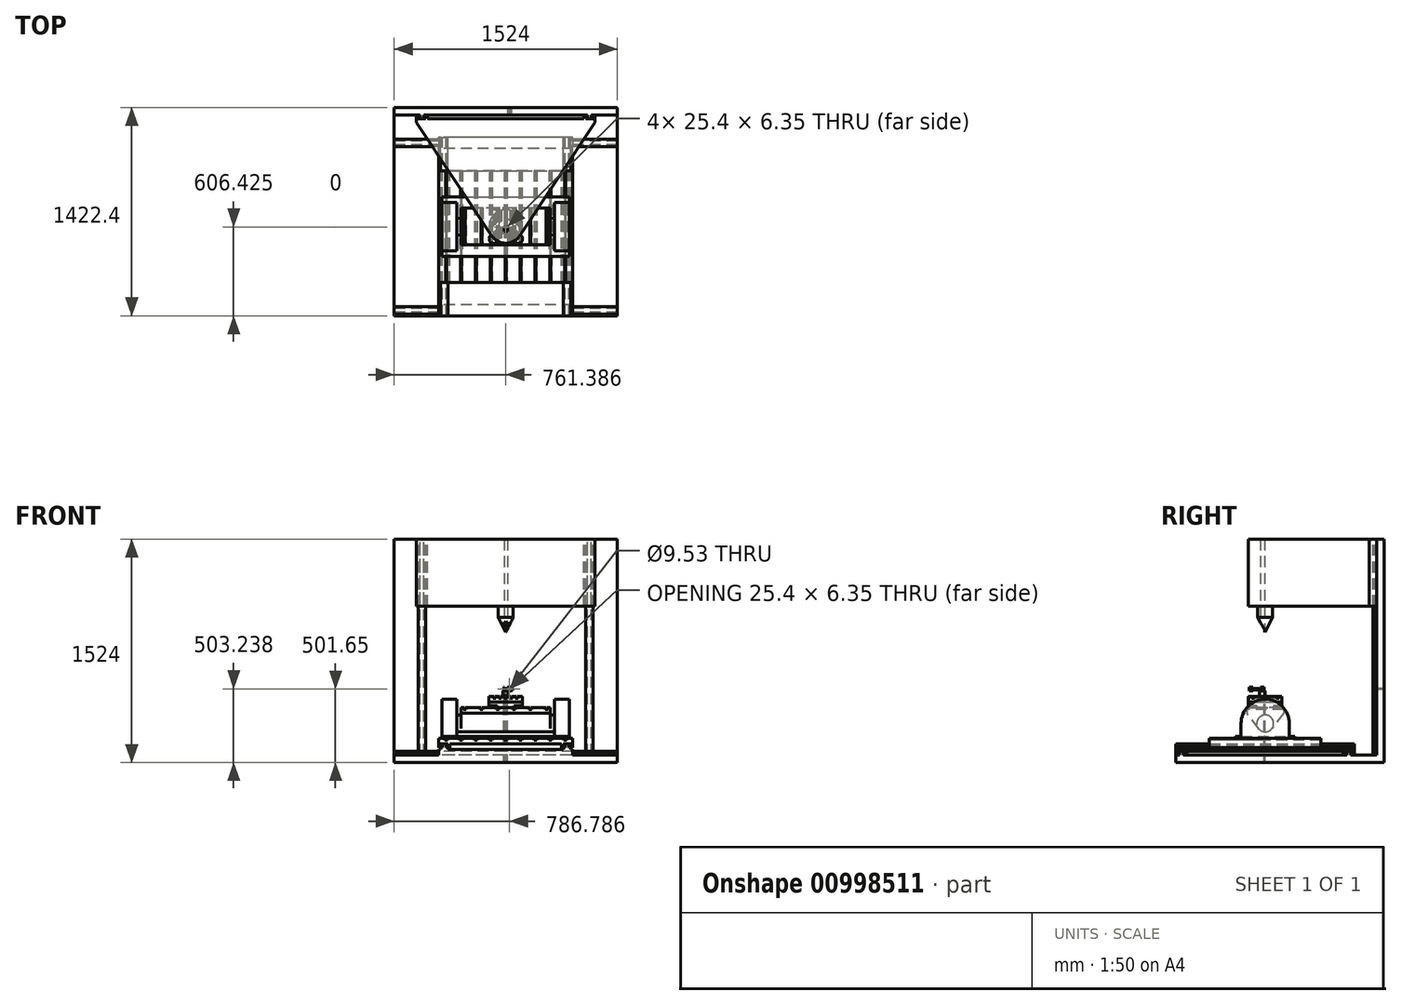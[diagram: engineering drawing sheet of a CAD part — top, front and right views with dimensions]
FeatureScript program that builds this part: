
annotation { "Feature Type Name" : "Feature", "Feature Type Description" : "" }
export const myFeature = defineFeature(function(context is Context, id is Id, definition is map)
    precondition{}
    {
        {
            var Q0;
            Q0=qCreatedBy(makeId("Right.planeOp"),FACE);
            var sketch = newSketch(context, id + "F0", { "sketchPlane" : qUnion([Q0])});
            skLineSegment(sketch, "E0.bottom", {"start": v(-596.9, 0) * mm, "end": v(-546.1, 0) * mm});
            skLineSegment(sketch, "E0.top", {"start": v(-596.9, 12.7) * mm, "end": v(-546.1, 12.7) * mm});
            skLineSegment(sketch, "E0.left", {"start": v(-596.9, 0) * mm, "end": v(-596.9, 12.7) * mm});
            skLineSegment(sketch, "E0.right", {"start": v(-546.1, 0) * mm, "end": v(-546.1, 12.7) * mm});
            skLineSegment(sketch, "E1", {"start": v(0, 50.8) * mm, "end": v(0, 0) * mm, "construction": true});
            skLineSegment(sketch, "E2.bottom", {"start": v(-584.2, 0) * mm, "end": v(-558.8, 0) * mm});
            skLineSegment(sketch, "E2.top", {"start": v(-584.2, -12.7) * mm, "end": v(-558.8, -12.7) * mm});
            skLineSegment(sketch, "E2.left", {"start": v(-584.2, 0) * mm, "end": v(-584.2, -12.7) * mm});
            skLineSegment(sketch, "E2.right", {"start": v(-558.8, 0) * mm, "end": v(-558.8, -12.7) * mm});
            skLineSegment(sketch, "E3.MirrorCS", {"start": v(558.8, 0) * mm, "end": v(558.8, -12.7) * mm});
            skLineSegment(sketch, "E4.MirrorCS", {"start": v(584.2, -12.7) * mm, "end": v(558.8, -12.7) * mm});
            skLineSegment(sketch, "E5.MirrorCS", {"start": v(584.2, 0) * mm, "end": v(558.8, 0) * mm});
            skLineSegment(sketch, "E6.MirrorCS", {"start": v(596.9, 0) * mm, "end": v(546.1, 0) * mm});
            skLineSegment(sketch, "E7.MirrorCS", {"start": v(596.9, 0) * mm, "end": v(596.9, 12.7) * mm});
            skLineSegment(sketch, "E8.MirrorCS", {"start": v(546.1, 0) * mm, "end": v(546.1, 12.7) * mm});
            skLineSegment(sketch, "E9.MirrorCS", {"start": v(584.2, 0) * mm, "end": v(584.2, -12.7) * mm});
            skLineSegment(sketch, "E10.MirrorCS", {"start": v(596.9, 12.7) * mm, "end": v(546.1, 12.7) * mm});
            skLineSegment(sketch, "E11.bottom", {"start": v(-609.6, -12.7) * mm, "end": v(609.6, -12.7) * mm});
            skLineSegment(sketch, "E11.top", {"start": v(-609.6, -63.5) * mm, "end": v(609.6, -63.5) * mm});
            skLineSegment(sketch, "E11.left", {"start": v(-609.6, -12.7) * mm, "end": v(-609.6, -63.5) * mm});
            skLineSegment(sketch, "E11.right", {"start": v(609.6, -12.7) * mm, "end": v(609.6, -63.5) * mm});
            skSolve(sketch);
        }
        {
            var Q0;
            {var subQ6=sQuery(id+"F0.wireOp",EDGE,"E2.top");var subQ7=makeQuery(id+"F0.imprint","IMPRINT",EDGE,{"derivedFrom":subQ6});var subQ10=sQuery(id+"F0.wireOp",EDGE,"E5.MirrorCS");var subQ11=sQuery(id+"F0.wireOp",EDGE,"E3.MirrorCS");var subQ14=makeQuery(id+"F0.imprint","IMPRINT",EDGE,{"derivedFrom":subQ10});Q0=qUnion([makeQuery(id+"F0.imprint","IMPRINT",FACE,{"disambiguationData":[TD([[subQ7,-1.0]])]}),makeQuery(id+"F0.imprint","IMPRINT",FACE,{"disambiguationData":[TD([[makeQuery(id+"F0.imprint","IMPRINT",EDGE,{"derivedFrom":sQuery(id+"F0.wireOp",EDGE,"E0.top")}),-1.0]])]}),makeQuery(id+"F0.imprint","IMPRINT",FACE,{"disambiguationData":[TD([[makeQuery(id+"F0.imprint","IMPRINT",EDGE,{"derivedFrom":subQ11}),1.0]])]}),makeQuery(id+"F0.imprint","IMPRINT",FACE,{"disambiguationData":[TD([[subQ14,-1.0]])]}),makeQuery(id+"F0.imprint","IMPRINT",FACE,{"disambiguationData":[TD([[subQ7,1.0]])]})]);}
            extrude(context, id + "F1", {"entities" : qUnion([Q0]), "depth" : 1524 * mm, "offsetDistance" : 25.4 * mm, "symmetric" : true});
        }
        {
            var Q0;
            Q0=qCreatedBy(makeId("Right.planeOp"),FACE);
            var sketch = newSketch(context, id + "F2", { "sketchPlane" : qUnion([Q0])});
            skLineSegment(sketch, "E12.0", {"start": v(-609.6, -12.7) * mm, "end": v(-584.2, -12.7) * mm});
            skLineSegment(sketch, "E13.0", {"start": v(-584.2, 0) * mm, "end": v(-584.2, -12.7) * mm});
            skLineSegment(sketch, "E14.0", {"start": v(-596.9, 0) * mm, "end": v(-584.2, 0) * mm});
            skLineSegment(sketch, "E15.0", {"start": v(-596.9, 0) * mm, "end": v(-596.9, 12.7) * mm});
            skLineSegment(sketch, "E16.0", {"start": v(-596.9, 12.7) * mm, "end": v(-546.1, 12.7) * mm});
            skLineSegment(sketch, "E17.0", {"start": v(-546.1, 0) * mm, "end": v(-546.1, 12.7) * mm});
            skLineSegment(sketch, "E18.0", {"start": v(-558.8, 0) * mm, "end": v(-546.1, 0) * mm});
            skLineSegment(sketch, "E19.0", {"start": v(-558.8, 0) * mm, "end": v(-558.8, -12.7) * mm});
            skLineSegment(sketch, "E20.0", {"start": v(558.8, 0) * mm, "end": v(558.8, -12.7) * mm});
            skLineSegment(sketch, "E21.0", {"start": v(558.8, 0) * mm, "end": v(546.1, 0) * mm});
            skLineSegment(sketch, "E22.0", {"start": v(546.1, 0) * mm, "end": v(546.1, 12.7) * mm});
            skLineSegment(sketch, "E23.0", {"start": v(596.9, 12.7) * mm, "end": v(546.1, 12.7) * mm});
            skLineSegment(sketch, "E24.0", {"start": v(596.9, 0) * mm, "end": v(596.9, 12.7) * mm});
            skLineSegment(sketch, "E25.0", {"start": v(596.9, 0) * mm, "end": v(584.2, 0) * mm});
            skLineSegment(sketch, "E26.0", {"start": v(584.2, 0) * mm, "end": v(584.2, -12.7) * mm});
            skLineSegment(sketch, "E27.0", {"start": v(584.2, -12.7) * mm, "end": v(609.6, -12.7) * mm});
            skLineSegment(sketch, "E28", {"start": v(-609.6, -12.7) * mm, "end": v(-609.6, 25.4) * mm});
            skLineSegment(sketch, "E29", {"start": v(-609.6, 25.4) * mm, "end": v(609.6, 25.4) * mm});
            skLineSegment(sketch, "E30", {"start": v(609.6, 25.4) * mm, "end": v(609.6, -12.7) * mm});
            skLineSegment(sketch, "E31", {"start": v(-558.8, -12.7) * mm, "end": v(-533.4, -12.7) * mm});
            skLineSegment(sketch, "E32", {"start": v(-533.4, -12.7) * mm, "end": v(-533.4, 12.7) * mm});
            skLineSegment(sketch, "E33", {"start": v(-533.4, 12.7) * mm, "end": v(533.4, 12.7) * mm});
            skLineSegment(sketch, "E34", {"start": v(533.4, 12.7) * mm, "end": v(533.4, -12.7) * mm});
            skLineSegment(sketch, "E35", {"start": v(533.4, -12.7) * mm, "end": v(558.8, -12.7) * mm});
            skSolve(sketch);
        }
        {
            var Q0;
            Q0 = qSketchRegion(id + "F2", true);
            extrude(context, id + "F3", {"entities" : qUnion([Q0]), "depth" : 914.4 * mm, "offsetDistance" : 25.4 * mm, "symmetric" : true});
        }
        {
            var Q0;
            Q0=qCreatedBy(makeId("Front.planeOp"),FACE);
            var sketch = newSketch(context, id + "F4", { "sketchPlane" : qUnion([Q0])});
            skLineSegment(sketch, "E36", {"start": v(0, 0) * mm, "end": v(0, 50.8) * mm, "construction": true});
            skPoint(sketch, "E37.0", {"position": v(-444.5, 25.4) * mm});
            skLineSegment(sketch, "E38", {"start": v(-444.5, 25.4) * mm, "end": v(-444.5, 38.1) * mm});
            skLineSegment(sketch, "E39", {"start": v(-444.5, 38.1) * mm, "end": v(-431.8, 38.1) * mm});
            skLineSegment(sketch, "E40", {"start": v(-431.8, 38.1) * mm, "end": v(-431.8, 50.8) * mm});
            skLineSegment(sketch, "E41", {"start": v(-431.8, 50.8) * mm, "end": v(-444.5, 50.8) * mm});
            skLineSegment(sketch, "E42", {"start": v(-444.5, 50.8) * mm, "end": v(-444.5, 63.5) * mm});
            skLineSegment(sketch, "E43", {"start": v(-444.5, 63.5) * mm, "end": v(-393.7, 63.5) * mm});
            skLineSegment(sketch, "E44", {"start": v(-393.7, 63.5) * mm, "end": v(-393.7, 50.8) * mm});
            skLineSegment(sketch, "E45", {"start": v(-393.7, 50.8) * mm, "end": v(-406.4, 50.8) * mm});
            skLineSegment(sketch, "E46", {"start": v(-406.4, 50.8) * mm, "end": v(-406.4, 38.1) * mm});
            skLineSegment(sketch, "E47", {"start": v(-406.4, 38.1) * mm, "end": v(-393.7, 38.1) * mm});
            skLineSegment(sketch, "E48", {"start": v(-393.7, 38.1) * mm, "end": v(-393.7, 25.4) * mm});
            skLineSegment(sketch, "E49", {"start": v(-393.7, 25.4) * mm, "end": v(-444.5, 25.4) * mm});
            skLineSegment(sketch, "E50.MirrorCS", {"start": v(393.7, 50.8) * mm, "end": v(406.4, 50.8) * mm});
            skLineSegment(sketch, "E51.MirrorCS", {"start": v(431.8, 50.8) * mm, "end": v(444.5, 50.8) * mm});
            skLineSegment(sketch, "E52.MirrorCS", {"start": v(406.4, 38.1) * mm, "end": v(393.7, 38.1) * mm});
            skLineSegment(sketch, "E53.MirrorCS", {"start": v(444.5, 38.1) * mm, "end": v(431.8, 38.1) * mm});
            skLineSegment(sketch, "E54.MirrorCS", {"start": v(393.7, 63.5) * mm, "end": v(393.7, 50.8) * mm});
            skLineSegment(sketch, "E55.MirrorCS", {"start": v(444.5, 25.4) * mm, "end": v(444.5, 38.1) * mm});
            skLineSegment(sketch, "E56.MirrorCS", {"start": v(444.5, 50.8) * mm, "end": v(444.5, 63.5) * mm});
            skLineSegment(sketch, "E57.MirrorCS", {"start": v(406.4, 50.8) * mm, "end": v(406.4, 38.1) * mm});
            skLineSegment(sketch, "E58.MirrorCS", {"start": v(431.8, 38.1) * mm, "end": v(431.8, 50.8) * mm});
            skLineSegment(sketch, "E59.MirrorCS", {"start": v(393.7, 38.1) * mm, "end": v(393.7, 25.4) * mm});
            skLineSegment(sketch, "E60.MirrorCS", {"start": v(393.7, 25.4) * mm, "end": v(444.5, 25.4) * mm});
            skPoint(sketch, "E61.MirrorP", {"position": v(444.5, 25.4) * mm});
            skLineSegment(sketch, "E62.MirrorCS", {"start": v(444.5, 63.5) * mm, "end": v(393.7, 63.5) * mm});
            skSolve(sketch);
        }
        {
            var Q0;
            Q0 = qSketchRegion(id + "F4", true);
            extrude(context, id + "F5", {"entities" : qUnion([Q0]), "operationType" : NewBodyOperationType.ADD, "depth" : 1219.2 * mm, "offsetDistance" : 25.4 * mm, "symmetric" : true});
        }
        {
            var Q0;
            Q0=qCreatedBy(makeId("Front.planeOp"),FACE);
            var sketch = newSketch(context, id + "F6", { "sketchPlane" : qUnion([Q0])});
            skLineSegment(sketch, "E63.0", {"start": v(-431.8, 38.1) * mm, "end": v(-431.8, 50.8) * mm});
            skLineSegment(sketch, "E64.0", {"start": v(-431.8, 50.8) * mm, "end": v(-444.5, 50.8) * mm});
            skLineSegment(sketch, "E65.0", {"start": v(-444.5, 50.8) * mm, "end": v(-444.5, 63.5) * mm});
            skLineSegment(sketch, "E66.0", {"start": v(-444.5, 63.5) * mm, "end": v(-393.7, 63.5) * mm});
            skLineSegment(sketch, "E67.0", {"start": v(-393.7, 63.5) * mm, "end": v(-393.7, 50.8) * mm});
            skLineSegment(sketch, "E68.0", {"start": v(-393.7, 50.8) * mm, "end": v(-406.4, 50.8) * mm});
            skLineSegment(sketch, "E69.0", {"start": v(-406.4, 50.8) * mm, "end": v(-406.4, 38.1) * mm});
            skLineSegment(sketch, "E70.0", {"start": v(406.4, 50.8) * mm, "end": v(406.4, 38.1) * mm});
            skLineSegment(sketch, "E71.0", {"start": v(393.7, 50.8) * mm, "end": v(406.4, 50.8) * mm});
            skLineSegment(sketch, "E72.0", {"start": v(393.7, 63.5) * mm, "end": v(393.7, 50.8) * mm});
            skLineSegment(sketch, "E73.0", {"start": v(444.5, 63.5) * mm, "end": v(393.7, 63.5) * mm});
            skLineSegment(sketch, "E74.0", {"start": v(444.5, 50.8) * mm, "end": v(444.5, 63.5) * mm});
            skLineSegment(sketch, "E75.0", {"start": v(431.8, 50.8) * mm, "end": v(444.5, 50.8) * mm});
            skLineSegment(sketch, "E76.0", {"start": v(431.8, 38.1) * mm, "end": v(431.8, 50.8) * mm});
            skLineSegment(sketch, "E77", {"start": v(-431.8, 38.1) * mm, "end": v(-457.2, 38.1) * mm});
            skLineSegment(sketch, "E78", {"start": v(-457.2, 38.1) * mm, "end": v(-457.2, 101.6) * mm});
            skLineSegment(sketch, "E79", {"start": v(-457.2, 101.6) * mm, "end": v(457.2, 101.6) * mm});
            skLineSegment(sketch, "E80", {"start": v(457.2, 101.6) * mm, "end": v(457.2, 38.1) * mm});
            skLineSegment(sketch, "E81", {"start": v(457.2, 38.1) * mm, "end": v(431.8, 38.1) * mm});
            skLineSegment(sketch, "E82", {"start": v(406.4, 38.1) * mm, "end": v(381, 38.1) * mm});
            skLineSegment(sketch, "E83", {"start": v(381, 38.1) * mm, "end": v(381, 63.5) * mm});
            skLineSegment(sketch, "E84", {"start": v(381, 63.5) * mm, "end": v(-381, 63.5) * mm});
            skLineSegment(sketch, "E85", {"start": v(-381, 63.5) * mm, "end": v(-381, 38.1) * mm});
            skLineSegment(sketch, "E86", {"start": v(-381, 38.1) * mm, "end": v(-406.4, 38.1) * mm});
            skSolve(sketch);
        }
        {
            var Q0;
            Q0 = qSketchRegion(id + "F6", true);
            extrude(context, id + "F7", {"entities" : qUnion([Q0]), "depth" : 762 * mm, "offsetDistance" : 25.4 * mm, "symmetric" : true});
        }
        {
            var Q0;
            Q0=qCreatedBy(makeId("Front.planeOp"),FACE);
            var sketch = newSketch(context, id + "F8", { "sketchPlane" : qUnion([Q0])});
            skLineSegment(sketch, "E87.0", {"start": v(-457.2, 101.6) * mm, "end": v(457.2, 101.6) * mm, "construction": true});
            skLineSegment(sketch, "E88", {"start": v(-409.58, 101.6) * mm, "end": v(-409.58, 95.25) * mm});
            skLineSegment(sketch, "E89", {"start": v(-409.58, 95.25) * mm, "end": v(-415.93, 95.25) * mm});
            skLineSegment(sketch, "E90", {"start": v(-415.93, 95.25) * mm, "end": v(-415.93, 88.9) * mm});
            skLineSegment(sketch, "E91", {"start": v(-415.93, 88.9) * mm, "end": v(-396.88, 88.9) * mm});
            skLineSegment(sketch, "E92", {"start": v(-396.88, 88.9) * mm, "end": v(-396.88, 95.25) * mm});
            skLineSegment(sketch, "E93", {"start": v(-396.88, 95.25) * mm, "end": v(-403.23, 95.25) * mm});
            skLineSegment(sketch, "E94", {"start": v(-403.23, 95.25) * mm, "end": v(-403.23, 101.6) * mm});
            skLineSegment(sketch, "E95", {"start": v(-409.58, 101.6) * mm, "end": v(-403.23, 101.6) * mm});
            skLineSegment(sketch, "E96.1.0.0", {"start": v(-301.62, 95.25) * mm, "end": v(-301.62, 101.6) * mm});
            skLineSegment(sketch, "E96.1.0.1", {"start": v(-314.33, 88.9) * mm, "end": v(-295.27, 88.9) * mm});
            skLineSegment(sketch, "E96.1.0.2", {"start": v(-307.98, 101.6) * mm, "end": v(-307.98, 95.25) * mm});
            skLineSegment(sketch, "E96.1.0.3", {"start": v(-307.98, 95.25) * mm, "end": v(-314.33, 95.25) * mm});
            skLineSegment(sketch, "E96.1.0.4", {"start": v(-314.33, 95.25) * mm, "end": v(-314.33, 88.9) * mm});
            skLineSegment(sketch, "E96.1.0.5", {"start": v(-295.27, 95.25) * mm, "end": v(-301.62, 95.25) * mm});
            skLineSegment(sketch, "E96.1.0.6", {"start": v(-307.98, 101.6) * mm, "end": v(-301.62, 101.6) * mm});
            skLineSegment(sketch, "E96.1.0.7", {"start": v(-295.27, 88.9) * mm, "end": v(-295.27, 95.25) * mm});
            skLineSegment(sketch, "E96.2.0.0", {"start": v(-200.02, 95.25) * mm, "end": v(-200.02, 101.6) * mm});
            skLineSegment(sketch, "E96.2.0.1", {"start": v(-212.72, 88.9) * mm, "end": v(-193.67, 88.9) * mm});
            skLineSegment(sketch, "E96.2.0.2", {"start": v(-206.37, 101.6) * mm, "end": v(-206.37, 95.25) * mm});
            skLineSegment(sketch, "E96.2.0.3", {"start": v(-206.37, 95.25) * mm, "end": v(-212.72, 95.25) * mm});
            skLineSegment(sketch, "E96.2.0.4", {"start": v(-212.72, 95.25) * mm, "end": v(-212.72, 88.9) * mm});
            skLineSegment(sketch, "E96.2.0.5", {"start": v(-193.67, 95.25) * mm, "end": v(-200.02, 95.25) * mm});
            skLineSegment(sketch, "E96.2.0.6", {"start": v(-206.37, 101.6) * mm, "end": v(-200.02, 101.6) * mm});
            skLineSegment(sketch, "E96.2.0.7", {"start": v(-193.67, 88.9) * mm, "end": v(-193.67, 95.25) * mm});
            skLineSegment(sketch, "E96.3.0.0", {"start": v(-98.42, 95.25) * mm, "end": v(-98.42, 101.6) * mm});
            skLineSegment(sketch, "E96.3.0.1", {"start": v(-111.12, 88.9) * mm, "end": v(-92.07, 88.9) * mm});
            skLineSegment(sketch, "E96.3.0.2", {"start": v(-104.77, 101.6) * mm, "end": v(-104.77, 95.25) * mm});
            skLineSegment(sketch, "E96.3.0.3", {"start": v(-104.77, 95.25) * mm, "end": v(-111.12, 95.25) * mm});
            skLineSegment(sketch, "E96.3.0.4", {"start": v(-111.12, 95.25) * mm, "end": v(-111.12, 88.9) * mm});
            skLineSegment(sketch, "E96.3.0.5", {"start": v(-92.07, 95.25) * mm, "end": v(-98.42, 95.25) * mm});
            skLineSegment(sketch, "E96.3.0.6", {"start": v(-104.77, 101.6) * mm, "end": v(-98.42, 101.6) * mm});
            skLineSegment(sketch, "E96.3.0.7", {"start": v(-92.07, 88.9) * mm, "end": v(-92.07, 95.25) * mm});
            skLineSegment(sketch, "E96.4.0.0", {"start": v(3.18, 95.25) * mm, "end": v(3.18, 101.6) * mm});
            skLineSegment(sketch, "E96.4.0.1", {"start": v(-9.52, 88.9) * mm, "end": v(9.53, 88.9) * mm});
            skLineSegment(sketch, "E96.4.0.2", {"start": v(-3.17, 101.6) * mm, "end": v(-3.17, 95.25) * mm});
            skLineSegment(sketch, "E96.4.0.3", {"start": v(-3.17, 95.25) * mm, "end": v(-9.52, 95.25) * mm});
            skLineSegment(sketch, "E96.4.0.4", {"start": v(-9.52, 95.25) * mm, "end": v(-9.52, 88.9) * mm});
            skLineSegment(sketch, "E96.4.0.5", {"start": v(9.53, 95.25) * mm, "end": v(3.18, 95.25) * mm});
            skLineSegment(sketch, "E96.4.0.6", {"start": v(-3.17, 101.6) * mm, "end": v(3.18, 101.6) * mm});
            skLineSegment(sketch, "E96.4.0.7", {"start": v(9.53, 88.9) * mm, "end": v(9.53, 95.25) * mm});
            skLineSegment(sketch, "E96.5.0.0", {"start": v(104.78, 95.25) * mm, "end": v(104.78, 101.6) * mm});
            skLineSegment(sketch, "E96.5.0.1", {"start": v(92.08, 88.9) * mm, "end": v(111.13, 88.9) * mm});
            skLineSegment(sketch, "E96.5.0.2", {"start": v(98.43, 101.6) * mm, "end": v(98.43, 95.25) * mm});
            skLineSegment(sketch, "E96.5.0.3", {"start": v(98.43, 95.25) * mm, "end": v(92.08, 95.25) * mm});
            skLineSegment(sketch, "E96.5.0.4", {"start": v(92.08, 95.25) * mm, "end": v(92.08, 88.9) * mm});
            skLineSegment(sketch, "E96.5.0.5", {"start": v(111.13, 95.25) * mm, "end": v(104.78, 95.25) * mm});
            skLineSegment(sketch, "E96.5.0.6", {"start": v(98.43, 101.6) * mm, "end": v(104.78, 101.6) * mm});
            skLineSegment(sketch, "E96.5.0.7", {"start": v(111.13, 88.9) * mm, "end": v(111.13, 95.25) * mm});
            skLineSegment(sketch, "E96.6.0.0", {"start": v(206.38, 95.25) * mm, "end": v(206.38, 101.6) * mm});
            skLineSegment(sketch, "E96.6.0.1", {"start": v(193.68, 88.9) * mm, "end": v(212.73, 88.9) * mm});
            skLineSegment(sketch, "E96.6.0.2", {"start": v(200.03, 101.6) * mm, "end": v(200.03, 95.25) * mm});
            skLineSegment(sketch, "E96.6.0.3", {"start": v(200.03, 95.25) * mm, "end": v(193.68, 95.25) * mm});
            skLineSegment(sketch, "E96.6.0.4", {"start": v(193.68, 95.25) * mm, "end": v(193.68, 88.9) * mm});
            skLineSegment(sketch, "E96.6.0.5", {"start": v(212.73, 95.25) * mm, "end": v(206.38, 95.25) * mm});
            skLineSegment(sketch, "E96.6.0.6", {"start": v(200.03, 101.6) * mm, "end": v(206.38, 101.6) * mm});
            skLineSegment(sketch, "E96.6.0.7", {"start": v(212.73, 88.9) * mm, "end": v(212.73, 95.25) * mm});
            skLineSegment(sketch, "E96.7.0.0", {"start": v(307.98, 95.25) * mm, "end": v(307.98, 101.6) * mm});
            skLineSegment(sketch, "E96.7.0.1", {"start": v(295.28, 88.9) * mm, "end": v(314.33, 88.9) * mm});
            skLineSegment(sketch, "E96.7.0.2", {"start": v(301.63, 101.6) * mm, "end": v(301.63, 95.25) * mm});
            skLineSegment(sketch, "E96.7.0.3", {"start": v(301.63, 95.25) * mm, "end": v(295.28, 95.25) * mm});
            skLineSegment(sketch, "E96.7.0.4", {"start": v(295.28, 95.25) * mm, "end": v(295.28, 88.9) * mm});
            skLineSegment(sketch, "E96.7.0.5", {"start": v(314.33, 95.25) * mm, "end": v(307.98, 95.25) * mm});
            skLineSegment(sketch, "E96.7.0.6", {"start": v(301.63, 101.6) * mm, "end": v(307.98, 101.6) * mm});
            skLineSegment(sketch, "E96.7.0.7", {"start": v(314.33, 88.9) * mm, "end": v(314.33, 95.25) * mm});
            skLineSegment(sketch, "E96.8.0.0", {"start": v(409.58, 95.25) * mm, "end": v(409.58, 101.6) * mm});
            skLineSegment(sketch, "E96.8.0.1", {"start": v(396.88, 88.9) * mm, "end": v(415.93, 88.9) * mm});
            skLineSegment(sketch, "E96.8.0.2", {"start": v(403.23, 101.6) * mm, "end": v(403.23, 95.25) * mm});
            skLineSegment(sketch, "E96.8.0.3", {"start": v(403.23, 95.25) * mm, "end": v(396.88, 95.25) * mm});
            skLineSegment(sketch, "E96.8.0.4", {"start": v(396.88, 95.25) * mm, "end": v(396.88, 88.9) * mm});
            skLineSegment(sketch, "E96.8.0.5", {"start": v(415.93, 95.25) * mm, "end": v(409.58, 95.25) * mm});
            skLineSegment(sketch, "E96.8.0.6", {"start": v(403.23, 101.6) * mm, "end": v(409.58, 101.6) * mm});
            skLineSegment(sketch, "E96.8.0.7", {"start": v(415.93, 88.9) * mm, "end": v(415.93, 95.25) * mm});
            skLineSegment(sketch, "E96.direction1", {"start": v(-415.93, 88.9) * mm, "end": v(-314.33, 88.9) * mm, "construction": true});
            skSolve(sketch);
        }
        {
            var Q0;
            Q0 = qSketchRegion(id + "F8", true);
            extrude(context, id + "F9", {"entities" : qUnion([Q0]), "operationType" : NewBodyOperationType.REMOVE, "endBound" : BoundingType.THROUGH_ALL, "oppositeDirection" : true, "depth" : 25.4 * mm, "offsetDistance" : 25.4 * mm, "hasSecondDirection" : true, "secondDirectionBound" : BoundingType.THROUGH_ALL, "secondDirectionOppositeDirection" : false, "secondDirectionDepth" : 25.4 * mm});
        }
        {
            var Q0;
            Q0=qCreatedBy(makeId("Front.planeOp"),FACE);
            var sketch = newSketch(context, id + "F10", { "sketchPlane" : qUnion([Q0])});
            skPoint(sketch, "E97.0", {"position": v(-457.2, 101.6) * mm});
            skPoint(sketch, "E98.0", {"position": v(457.2, 101.6) * mm});
            skLineSegment(sketch, "E99.bottom", {"start": v(-434.98, 101.6) * mm, "end": v(434.98, 101.6) * mm});
            skLineSegment(sketch, "E99.top", {"start": v(-434.98, 114.3) * mm, "end": v(434.98, 114.3) * mm});
            skLineSegment(sketch, "E99.left", {"start": v(-434.98, 101.6) * mm, "end": v(-434.98, 114.3) * mm});
            skLineSegment(sketch, "E99.right", {"start": v(434.98, 101.6) * mm, "end": v(434.98, 114.3) * mm});
            skSolve(sketch);
        }
        {
            var Q0;
            Q0 = qSketchRegion(id + "F10", true);
            extrude(context, id + "F11", {"entities" : qUnion([Q0]), "depth" : 406.4 * mm, "offsetDistance" : 25.4 * mm, "symmetric" : true});
        }
        {
            var Q0;
            Q0=makeQuery(id+"F11.opExtrude","SWEPT_FACE",FACE,{"disambiguationData":[OSD([sQuery(id+"F10.wireOp",EDGE,"E99.left")])]});
            var sketch = newSketch(context, id + "F12", { "sketchPlane" : qUnion([Q0])});
            skLineSegment(sketch, "E100", {"start": v(-165.1, 114.3) * mm, "end": v(-165.1, 203.2) * mm});
            skLineSegment(sketch, "E101", {"start": v(165.1, 203.2) * mm, "end": v(165.1, 114.3) * mm});
            skArc(sketch, "E102", {"start": v(-165.1, 203.2) * mm, "mid": v(0, 368.3) * mm, "end": v(165.1, 203.2) * mm});
            skLineSegment(sketch, "E103", {"start": v(165.1, 114.3) * mm, "end": v(-165.1, 114.3) * mm});
            skSolve(sketch);
        }
        {
            var Q0;
            Q0=makeQuery(id+"F11.opExtrude","SWEPT_FACE",FACE,{"disambiguationData":[OSD([sQuery(id+"F10.wireOp",EDGE,"E99.right")])]});
            var sketch = newSketch(context, id + "F13", { "sketchPlane" : qUnion([Q0])});
            skLineSegment(sketch, "E104.0", {"start": v(-165.1, 203.2) * mm, "end": v(-165.1, 114.3) * mm});
            skArc(sketch, "E105.0", {"start": v(165.1, 203.2) * mm, "mid": v(0, 368.3) * mm, "end": v(-165.1, 203.2) * mm});
            skLineSegment(sketch, "E106.0", {"start": v(165.1, 114.3) * mm, "end": v(165.1, 203.2) * mm});
            skLineSegment(sketch, "E107", {"start": v(-165.1, 114.3) * mm, "end": v(165.1, 114.3) * mm});
            skSolve(sketch);
        }
        {
            var Q0;
            Q0 = qSketchRegion(id + "F13", true);
            extrude(context, id + "F14", {"entities" : qUnion([Q0]), "operationType" : NewBodyOperationType.ADD, "oppositeDirection" : true, "depth" : 101.6 * mm, "offsetDistance" : 25.4 * mm});
        }
        {
            var Q0;
            Q0 = qSketchRegion(id + "F12", true);
            extrude(context, id + "F15", {"entities" : qUnion([Q0]), "operationType" : NewBodyOperationType.ADD, "oppositeDirection" : true, "depth" : 101.6 * mm, "offsetDistance" : 25.4 * mm});
        }
        {
            var Q0;
            Q0=qCreatedBy(makeId("Right.planeOp"),FACE);
            var sketch = newSketch(context, id + "F16", { "sketchPlane" : qUnion([Q0])});
            skArc(sketch, "E108.0", {"start": v(165.1, 203.2) * mm, "mid": v(0, 368.3) * mm, "end": v(-165.1, 203.2) * mm, "construction": true});
            skCircle(sketch, "E109", {"center": v(0, 203.2) * mm, "radius": 31.75 * mm});
            skSolve(sketch);
        }
        {
            var Q0;
            Q0 = qSketchRegion(id + "F16", true);
            extrude(context, id + "F17", {"entities" : qUnion([Q0]), "operationType" : NewBodyOperationType.REMOVE, "endBound" : BoundingType.THROUGH_ALL, "oppositeDirection" : true, "depth" : 25.4 * mm, "offsetDistance" : 25.4 * mm, "hasSecondDirection" : true, "secondDirectionBound" : BoundingType.THROUGH_ALL, "secondDirectionOppositeDirection" : false, "secondDirectionDepth" : 25.4 * mm});
        }
        {
            var Q0;
            Q0=qCreatedBy(makeId("Right.planeOp"),FACE);
            var sketch = newSketch(context, id + "F18", { "sketchPlane" : qUnion([Q0])});
            skArc(sketch, "E110.0", {"start": v(165.1, 203.2) * mm, "mid": v(0, 368.3) * mm, "end": v(-165.1, 203.2) * mm, "construction": true});
            skLineSegment(sketch, "E111.bottom", {"start": v(124.92, 311.15) * mm, "end": v(-124.92, 311.15) * mm});
            skLineSegment(sketch, "E111.top", {"start": v(124.92, 273.05) * mm, "end": v(-124.92, 273.05) * mm});
            skLineSegment(sketch, "E111.left", {"start": v(124.92, 311.15) * mm, "end": v(124.92, 273.05) * mm});
            skLineSegment(sketch, "E111.right", {"start": v(-124.92, 311.15) * mm, "end": v(-124.92, 273.05) * mm});
            skCircle(sketch, "E112.0", {"center": v(0, 203.2) * mm, "radius": 31.75 * mm});
            skCircle(sketch, "E113", {"center": v(0, 203.2) * mm, "radius": 57.15 * mm});
            skLineSegment(sketch, "E114", {"start": v(124.92, 273.05) * mm, "end": v(45.49, 168.6) * mm});
            skLineSegment(sketch, "E115", {"start": v(-45.49, 168.6) * mm, "end": v(-124.92, 273.05) * mm});
            skPoint(sketch, "E116", {"position": v(0, 260.35) * mm});
            skSolve(sketch);
        }
        {
            var Q0;
            Q0=makeQuery(id+"F18.imprint","IMPRINT",FACE,{"disambiguationData":[TD([[makeQuery(id+"F18.imprint","IMPRINT",EDGE,{"derivedFrom":sQuery(id+"F18.wireOp",EDGE,"E112.0")}),1.0]])]});
            var Q1;
            Q1=makeQuery(id+"F15.boolean.opBoolean","MERGE",FACE,{"derivedFrom":[makeQuery(id+"F11.opExtrude","SWEPT_FACE",FACE,{"disambiguationData":[OSD([sQuery(id+"F10.wireOp",EDGE,"E99.left")])]}),makeQuery(id+"F15.opExtrude","CAP_FACE",FACE,{"disambiguationData":[OSD([sQuery(id+"F12.wireOp",EDGE,"E100"),sQuery(id+"F12.wireOp",EDGE,"E101"),sQuery(id+"F12.wireOp",EDGE,"E102"),sQuery(id+"F12.wireOp",EDGE,"E103")])],"isStart":true})]});
            var Q2;
            Q2=makeQuery(id+"F14.boolean.opBoolean","MERGE",FACE,{"derivedFrom":[makeQuery(id+"F11.opExtrude","SWEPT_FACE",FACE,{"disambiguationData":[OSD([sQuery(id+"F10.wireOp",EDGE,"E99.right")])]}),makeQuery(id+"F14.opExtrude","CAP_FACE",FACE,{"disambiguationData":[OSD([sQuery(id+"F13.wireOp",EDGE,"E104.0"),sQuery(id+"F13.wireOp",EDGE,"E105.0"),sQuery(id+"F13.wireOp",EDGE,"E106.0"),sQuery(id+"F13.wireOp",EDGE,"E107")])],"isStart":true})]});
            extrude(context, id + "F19", {"entities" : qUnion([Q0]), "endBound" : BoundingType.UP_TO_SURFACE, "oppositeDirection" : true, "depth" : 25.4 * mm, "endBoundEntityFace" : qUnion([Q1]), "offsetDistance" : 25.4 * mm, "hasSecondDirection" : true, "secondDirectionBound" : BoundingType.UP_TO_SURFACE, "secondDirectionOppositeDirection" : false, "secondDirectionDepth" : 25.4 * mm, "secondDirectionBoundEntityFace" : qUnion([Q2])});
        }
        {
            var Q0;
            Q0=makeQuery(id+"F18.imprint","IMPRINT",FACE,{"disambiguationData":[TD([[makeQuery(id+"F18.imprint","IMPRINT",EDGE,{"derivedFrom":sQuery(id+"F18.wireOp",EDGE,"E112.0")}),-1.0]])]});
            var Q1;
            Q1=makeQuery(id+"F14.opExtrude","CAP_FACE",FACE,{"disambiguationData":[OSD([sQuery(id+"F13.wireOp",EDGE,"E104.0"),sQuery(id+"F13.wireOp",EDGE,"E105.0"),sQuery(id+"F13.wireOp",EDGE,"E106.0"),sQuery(id+"F13.wireOp",EDGE,"E107")])],"isStart":false});
            var Q2;
            Q2=makeQuery(id+"F15.opExtrude","CAP_FACE",FACE,{"disambiguationData":[OSD([sQuery(id+"F12.wireOp",EDGE,"E100"),sQuery(id+"F12.wireOp",EDGE,"E101"),sQuery(id+"F12.wireOp",EDGE,"E102"),sQuery(id+"F12.wireOp",EDGE,"E103")])],"isStart":false});
            extrude(context, id + "F20", {"entities" : qUnion([Q0]), "operationType" : NewBodyOperationType.ADD, "endBound" : BoundingType.UP_TO_SURFACE, "depth" : 25.4 * mm, "endBoundEntityFace" : qUnion([Q1]), "offsetDistance" : 25.4 * mm, "hasSecondDirection" : true, "secondDirectionBound" : BoundingType.UP_TO_SURFACE, "secondDirectionOppositeDirection" : true, "secondDirectionDepth" : 25.4 * mm, "secondDirectionBoundEntityFace" : qUnion([Q2])});
        }
        {
            var Q0;
            Q0=makeQuery(id+"F18.imprint","IMPRINT",FACE,{"disambiguationData":[TD([[makeQuery(id+"F18.imprint","IMPRINT",EDGE,{"derivedFrom":sQuery(id+"F18.wireOp",EDGE,"E111.top")}),1.0]])]});
            var Q1;
            Q1=makeQuery(id+"F18.imprint","IMPRINT",FACE,{"disambiguationData":[TD([[makeQuery(id+"F18.imprint","IMPRINT",EDGE,{"derivedFrom":sQuery(id+"F18.wireOp",EDGE,"E111.bottom")}),1.0]])]});
            extrude(context, id + "F21", {"entities" : qUnion([Q0, Q1]), "operationType" : NewBodyOperationType.ADD, "depth" : 609.6 * mm, "offsetDistance" : 25.4 * mm, "symmetric" : true});
        }
        {
            var Q0;
            Q0=qCreatedBy(makeId("Front.planeOp"),FACE);
            var sketch = newSketch(context, id + "F22", { "sketchPlane" : qUnion([Q0])});
            skLineSegment(sketch, "E117.0", {"start": v(304.8, 311.15) * mm, "end": v(-304.8, 311.15) * mm, "construction": true});
            skLineSegment(sketch, "E118", {"start": v(282.58, 311.15) * mm, "end": v(276.23, 311.15) * mm});
            skLineSegment(sketch, "E119", {"start": v(276.23, 311.15) * mm, "end": v(276.23, 304.8) * mm});
            skLineSegment(sketch, "E120", {"start": v(276.23, 304.8) * mm, "end": v(269.88, 304.8) * mm});
            skLineSegment(sketch, "E121", {"start": v(269.88, 304.8) * mm, "end": v(269.88, 298.45) * mm});
            skLineSegment(sketch, "E122", {"start": v(269.88, 298.45) * mm, "end": v(288.93, 298.45) * mm});
            skLineSegment(sketch, "E123", {"start": v(288.93, 298.45) * mm, "end": v(288.93, 304.8) * mm});
            skLineSegment(sketch, "E124", {"start": v(288.93, 304.8) * mm, "end": v(282.58, 304.8) * mm});
            skLineSegment(sketch, "E125", {"start": v(282.58, 304.8) * mm, "end": v(282.58, 311.15) * mm});
            skLineSegment(sketch, "E126.1.0.0", {"start": v(158.12, 298.45) * mm, "end": v(177.17, 298.45) * mm});
            skLineSegment(sketch, "E126.1.0.1", {"start": v(164.47, 311.15) * mm, "end": v(164.47, 304.8) * mm});
            skLineSegment(sketch, "E126.1.0.2", {"start": v(177.17, 304.8) * mm, "end": v(170.81, 304.8) * mm});
            skLineSegment(sketch, "E126.1.0.3", {"start": v(170.81, 304.8) * mm, "end": v(170.81, 311.15) * mm});
            skLineSegment(sketch, "E126.1.0.4", {"start": v(158.12, 304.8) * mm, "end": v(158.12, 298.45) * mm});
            skLineSegment(sketch, "E126.1.0.5", {"start": v(177.17, 298.45) * mm, "end": v(177.17, 304.8) * mm});
            skLineSegment(sketch, "E126.1.0.6", {"start": v(164.47, 304.8) * mm, "end": v(158.12, 304.8) * mm});
            skLineSegment(sketch, "E126.1.0.7", {"start": v(170.81, 311.15) * mm, "end": v(164.47, 311.15) * mm});
            skLineSegment(sketch, "E126.1.0.8", {"start": v(170.81, 311.15) * mm, "end": v(164.47, 311.15) * mm});
            skLineSegment(sketch, "E126.2.0.0", {"start": v(46.35, 298.45) * mm, "end": v(65.4, 298.45) * mm});
            skLineSegment(sketch, "E126.2.0.1", {"start": v(52.7, 311.15) * mm, "end": v(52.7, 304.8) * mm});
            skLineSegment(sketch, "E126.2.0.2", {"start": v(65.4, 304.8) * mm, "end": v(59.05, 304.8) * mm});
            skLineSegment(sketch, "E126.2.0.3", {"start": v(59.05, 304.8) * mm, "end": v(59.05, 311.15) * mm});
            skLineSegment(sketch, "E126.2.0.4", {"start": v(46.35, 304.8) * mm, "end": v(46.35, 298.45) * mm});
            skLineSegment(sketch, "E126.2.0.5", {"start": v(65.4, 298.45) * mm, "end": v(65.4, 304.8) * mm});
            skLineSegment(sketch, "E126.2.0.6", {"start": v(52.7, 304.8) * mm, "end": v(46.35, 304.8) * mm});
            skLineSegment(sketch, "E126.2.0.7", {"start": v(59.05, 311.15) * mm, "end": v(52.7, 311.15) * mm});
            skLineSegment(sketch, "E126.2.0.8", {"start": v(59.05, 311.15) * mm, "end": v(52.7, 311.15) * mm});
            skLineSegment(sketch, "E126.3.0.0", {"start": v(-65.4, 298.45) * mm, "end": v(-46.36, 298.45) * mm});
            skLineSegment(sketch, "E126.3.0.1", {"start": v(-59.06, 311.15) * mm, "end": v(-59.06, 304.8) * mm});
            skLineSegment(sketch, "E126.3.0.2", {"start": v(-46.36, 304.8) * mm, "end": v(-52.7, 304.8) * mm});
            skLineSegment(sketch, "E126.3.0.3", {"start": v(-52.7, 304.8) * mm, "end": v(-52.7, 311.15) * mm});
            skLineSegment(sketch, "E126.3.0.4", {"start": v(-65.4, 304.8) * mm, "end": v(-65.4, 298.45) * mm});
            skLineSegment(sketch, "E126.3.0.5", {"start": v(-46.36, 298.45) * mm, "end": v(-46.36, 304.8) * mm});
            skLineSegment(sketch, "E126.3.0.6", {"start": v(-59.06, 304.8) * mm, "end": v(-65.4, 304.8) * mm});
            skLineSegment(sketch, "E126.3.0.7", {"start": v(-52.7, 311.15) * mm, "end": v(-59.06, 311.15) * mm});
            skLineSegment(sketch, "E126.3.0.8", {"start": v(-52.7, 311.15) * mm, "end": v(-59.06, 311.15) * mm});
            skLineSegment(sketch, "E126.4.0.0", {"start": v(-177.17, 298.45) * mm, "end": v(-158.12, 298.45) * mm});
            skLineSegment(sketch, "E126.4.0.1", {"start": v(-170.82, 311.15) * mm, "end": v(-170.82, 304.8) * mm});
            skLineSegment(sketch, "E126.4.0.2", {"start": v(-158.12, 304.8) * mm, "end": v(-164.47, 304.8) * mm});
            skLineSegment(sketch, "E126.4.0.3", {"start": v(-164.47, 304.8) * mm, "end": v(-164.47, 311.15) * mm});
            skLineSegment(sketch, "E126.4.0.4", {"start": v(-177.17, 304.8) * mm, "end": v(-177.17, 298.45) * mm});
            skLineSegment(sketch, "E126.4.0.5", {"start": v(-158.12, 298.45) * mm, "end": v(-158.12, 304.8) * mm});
            skLineSegment(sketch, "E126.4.0.6", {"start": v(-170.82, 304.8) * mm, "end": v(-177.17, 304.8) * mm});
            skLineSegment(sketch, "E126.4.0.7", {"start": v(-164.47, 311.15) * mm, "end": v(-170.82, 311.15) * mm});
            skLineSegment(sketch, "E126.4.0.8", {"start": v(-164.47, 311.15) * mm, "end": v(-170.82, 311.15) * mm});
            skLineSegment(sketch, "E126.5.0.0", {"start": v(-288.93, 298.45) * mm, "end": v(-269.88, 298.45) * mm});
            skLineSegment(sketch, "E126.5.0.1", {"start": v(-282.58, 311.15) * mm, "end": v(-282.58, 304.8) * mm});
            skLineSegment(sketch, "E126.5.0.2", {"start": v(-269.88, 304.8) * mm, "end": v(-276.23, 304.8) * mm});
            skLineSegment(sketch, "E126.5.0.3", {"start": v(-276.23, 304.8) * mm, "end": v(-276.23, 311.15) * mm});
            skLineSegment(sketch, "E126.5.0.4", {"start": v(-288.93, 304.8) * mm, "end": v(-288.93, 298.45) * mm});
            skLineSegment(sketch, "E126.5.0.5", {"start": v(-269.88, 298.45) * mm, "end": v(-269.88, 304.8) * mm});
            skLineSegment(sketch, "E126.5.0.6", {"start": v(-282.58, 304.8) * mm, "end": v(-288.93, 304.8) * mm});
            skLineSegment(sketch, "E126.5.0.7", {"start": v(-276.23, 311.15) * mm, "end": v(-282.58, 311.15) * mm});
            skLineSegment(sketch, "E126.5.0.8", {"start": v(-276.23, 311.15) * mm, "end": v(-282.58, 311.15) * mm});
            skLineSegment(sketch, "E126.direction1", {"start": v(269.88, 298.45) * mm, "end": v(158.12, 298.45) * mm, "construction": true});
            skSolve(sketch);
        }
        {
            var Q0;
            Q0 = qSketchRegion(id + "F22", true);
            extrude(context, id + "F23", {"entities" : qUnion([Q0]), "operationType" : NewBodyOperationType.REMOVE, "endBound" : BoundingType.THROUGH_ALL, "oppositeDirection" : true, "depth" : 25.4 * mm, "offsetDistance" : 25.4 * mm, "hasSecondDirection" : true, "secondDirectionBound" : BoundingType.THROUGH_ALL, "secondDirectionOppositeDirection" : false, "secondDirectionDepth" : 25.4 * mm});
        }
        {
            var Q0;
            Q0=makeQuery(id+"F23.boolean.opBoolean","SPLIT",FACE,{"disambiguationData":[TD([makeQuery(id+"F23.opExtrude","SWEPT_FACE",FACE,{"disambiguationData":[OSD([sQuery(id+"F22.wireOp",EDGE,"E126.3.0.1")])]})])],"derivedFrom":makeQuery(id+"F21.opExtrude","SWEPT_FACE",FACE,{"disambiguationData":[OSD([sQuery(id+"F18.wireOp",EDGE,"E111.bottom")])]})});
            var sketch = newSketch(context, id + "F24", { "sketchPlane" : qUnion([Q0])});
            skPoint(sketch, "E127.0", {"position": v(-304.8, 124.92) * mm});
            skPoint(sketch, "E128.0", {"position": v(304.8, -124.92) * mm});
            skPoint(sketch, "E129.0", {"position": v(304.8, 124.92) * mm});
            skPoint(sketch, "E130.0", {"position": v(-304.8, -124.92) * mm});
            skLineSegment(sketch, "E131", {"start": v(-304.8, 124.92) * mm, "end": v(304.8, -124.92) * mm, "construction": true});
            skLineSegment(sketch, "E132", {"start": v(304.8, 124.92) * mm, "end": v(-304.8, -124.92) * mm, "construction": true});
            skCircle(sketch, "E133", {"center": v(0, 0) * mm, "radius": 114.3 * mm});
            skLineSegment(sketch, "E134", {"start": v(0, 0) * mm, "end": v(0, 114.3) * mm, "construction": true});
            skLineSegment(sketch, "E135.1.0", {"start": v(0, 0) * mm, "end": v(-29.58, 110.4) * mm, "construction": true});
            skLineSegment(sketch, "E135.2.0", {"start": v(0, 0) * mm, "end": v(-57.15, 98.99) * mm, "construction": true});
            skLineSegment(sketch, "E135.3.0", {"start": v(0, 0) * mm, "end": v(-80.82, 80.82) * mm, "construction": true});
            skLineSegment(sketch, "E135.4.0", {"start": v(0, 0) * mm, "end": v(-98.99, 57.15) * mm, "construction": true});
            skLineSegment(sketch, "E135.5.0", {"start": v(0, 0) * mm, "end": v(-110.4, 29.58) * mm, "construction": true});
            skLineSegment(sketch, "E135.6.0", {"start": v(0, 0) * mm, "end": v(-114.3, 0) * mm, "construction": true});
            skLineSegment(sketch, "E135.7.0", {"start": v(0, 0) * mm, "end": v(-110.4, -29.58) * mm, "construction": true});
            skLineSegment(sketch, "E135.8.0", {"start": v(0, 0) * mm, "end": v(-98.99, -57.15) * mm, "construction": true});
            skLineSegment(sketch, "E135.9.0", {"start": v(0, 0) * mm, "end": v(-80.82, -80.82) * mm, "construction": true});
            skLineSegment(sketch, "E135.10.0", {"start": v(0, 0) * mm, "end": v(-57.15, -98.99) * mm, "construction": true});
            skLineSegment(sketch, "E135.11.0", {"start": v(0, 0) * mm, "end": v(-29.58, -110.4) * mm, "construction": true});
            skLineSegment(sketch, "E135.12.0", {"start": v(0, 0) * mm, "end": v(0, -114.3) * mm, "construction": true});
            skLineSegment(sketch, "E135.13.0", {"start": v(0, 0) * mm, "end": v(29.58, -110.4) * mm, "construction": true});
            skLineSegment(sketch, "E135.14.0", {"start": v(0, 0) * mm, "end": v(57.15, -98.99) * mm, "construction": true});
            skLineSegment(sketch, "E135.15.0", {"start": v(0, 0) * mm, "end": v(80.82, -80.82) * mm, "construction": true});
            skLineSegment(sketch, "E135.16.0", {"start": v(0, 0) * mm, "end": v(98.99, -57.15) * mm, "construction": true});
            skLineSegment(sketch, "E135.17.0", {"start": v(0, 0) * mm, "end": v(110.4, -29.58) * mm, "construction": true});
            skLineSegment(sketch, "E135.18.0", {"start": v(0, 0) * mm, "end": v(114.3, 0) * mm, "construction": true});
            skLineSegment(sketch, "E135.19.0", {"start": v(0, 0) * mm, "end": v(110.4, 29.58) * mm, "construction": true});
            skLineSegment(sketch, "E135.20.0", {"start": v(0, 0) * mm, "end": v(98.99, 57.15) * mm, "construction": true});
            skLineSegment(sketch, "E135.21.0", {"start": v(0, 0) * mm, "end": v(80.82, 80.82) * mm, "construction": true});
            skLineSegment(sketch, "E135.22.0", {"start": v(0, 0) * mm, "end": v(57.15, 98.99) * mm, "construction": true});
            skLineSegment(sketch, "E135.23.0", {"start": v(0, 0) * mm, "end": v(29.58, 110.4) * mm, "construction": true});
            skArc(sketch, "E136", {"start": v(57.15, 98.99) * mm, "mid": v(105.33, 105.33) * mm, "end": v(98.99, 57.15) * mm});
            skArc(sketch, "E137", {"start": v(98.99, -57.15) * mm, "mid": v(105.33, -105.33) * mm, "end": v(57.15, -98.99) * mm});
            skArc(sketch, "E138", {"start": v(-57.15, 98.99) * mm, "mid": v(-105.33, 105.33) * mm, "end": v(-98.99, 57.15) * mm});
            skArc(sketch, "E139", {"start": v(-98.99, -57.15) * mm, "mid": v(-105.33, -105.33) * mm, "end": v(-57.15, -98.99) * mm});
            skSolve(sketch);
        }
        {
            var Q0;
            Q0 = qSketchRegion(id + "F24", true);
            extrude(context, id + "F25", {"entities" : qUnion([Q0]), "depth" : 12.7 * mm, "offsetDistance" : 25.4 * mm});
        }
        {
            var Q0;
            {var subQ1=sQuery(id+"F24.wireOp",EDGE,"E133");var subQ5=sQuery(id+"F24.wireOp",EDGE,"E136");var subQ6=makeQuery(id+"F24.imprint","INTERSECT",VERTEX,{"disambiguationData":[OD(0.0)],"derivedFrom":[subQ1,subQ5]});Q0=makeQuery(id+"F24.imprint","IMPRINT",FACE,{"disambiguationData":[TD([[makeQuery(id+"F24.imprint","IMPRINT",EDGE,{"disambiguationData":[TD([[subQ6,1.0]])],"derivedFrom":subQ1}),1.0]])]});}
            var Q1;
            {var subQ0=sQuery(id+"F24.wireOp",EDGE,"E133");var subQ4=makeQuery(id+"F24.imprint","INTERSECT",VERTEX,{"disambiguationData":[OD(0.0)],"derivedFrom":[subQ0,sQuery(id+"F24.wireOp",EDGE,"E138")]});Q1=makeQuery(id+"F24.imprint","IMPRINT",FACE,{"disambiguationData":[TD([[makeQuery(id+"F24.imprint","IMPRINT",EDGE,{"disambiguationData":[TD([[subQ4,1.0]])],"derivedFrom":subQ0}),1.0]])]});}
            var Q2;
            {var subQ0=sQuery(id+"F24.wireOp",EDGE,"E133");var subQ1=makeQuery(id+"F24.imprint","INTERSECT",VERTEX,{"disambiguationData":[OD(1.0)],"derivedFrom":[subQ0,sQuery(id+"F24.wireOp",EDGE,"E138")]});Q2=makeQuery(id+"F24.imprint","IMPRINT",FACE,{"disambiguationData":[TD([[makeQuery(id+"F24.imprint","IMPRINT",EDGE,{"disambiguationData":[TD([[subQ1,-1.0]])],"derivedFrom":subQ0}),1.0]])]});}
            var Q3;
            Q3=sQuery(id+"F24.wireOp",EDGE,"E133");
            extrude(context, id + "F26", {"entities" : qUnion([Q0, Q1, Q2]), "operationType" : NewBodyOperationType.ADD, "surfaceEntities" : qUnion([Q3]), "depth" : 38.1 * mm, "offsetDistance" : 25.4 * mm});
        }
        {
            var Q0;
            Q0=makeQuery(id+"F26.opExtrude","CAP_FACE",FACE,{"disambiguationData":[OSD([sQuery(id+"F24.wireOp",EDGE,"E133")])],"isStart":false});
            extrude(context, id + "F27", {"entities" : qUnion([Q0]), "depth" : 38.1 * mm, "offsetDistance" : 25.4 * mm});
        }
        {
            var Q0;
            Q0=qCreatedBy(makeId("Front.planeOp"),FACE);
            var sketch = newSketch(context, id + "F28", { "sketchPlane" : qUnion([Q0])});
            skLineSegment(sketch, "E140.0", {"start": v(-114.3, 387.35) * mm, "end": v(114.3, 387.35) * mm, "construction": true});
            skLineSegment(sketch, "E141", {"start": v(79.38, 387.35) * mm, "end": v(79.38, 381) * mm});
            skLineSegment(sketch, "E142", {"start": v(79.38, 381) * mm, "end": v(85.72, 381) * mm});
            skLineSegment(sketch, "E143", {"start": v(85.72, 381) * mm, "end": v(85.72, 374.65) * mm});
            skLineSegment(sketch, "E144", {"start": v(85.72, 374.65) * mm, "end": v(66.68, 374.65) * mm});
            skLineSegment(sketch, "E145", {"start": v(66.68, 374.65) * mm, "end": v(66.68, 381) * mm});
            skLineSegment(sketch, "E146", {"start": v(66.68, 381) * mm, "end": v(73.03, 381) * mm});
            skLineSegment(sketch, "E147", {"start": v(73.03, 381) * mm, "end": v(73.03, 387.35) * mm});
            skLineSegment(sketch, "E148", {"start": v(73.03, 387.35) * mm, "end": v(79.38, 387.35) * mm});
            skLineSegment(sketch, "E149.1.0.0", {"start": v(41.27, 387.35) * mm, "end": v(41.27, 381) * mm});
            skLineSegment(sketch, "E149.1.0.1", {"start": v(41.27, 381) * mm, "end": v(47.62, 381) * mm});
            skLineSegment(sketch, "E149.1.0.2", {"start": v(28.58, 381) * mm, "end": v(34.93, 381) * mm});
            skLineSegment(sketch, "E149.1.0.3", {"start": v(47.62, 381) * mm, "end": v(47.62, 374.65) * mm});
            skLineSegment(sketch, "E149.1.0.4", {"start": v(47.62, 374.65) * mm, "end": v(28.58, 374.65) * mm});
            skLineSegment(sketch, "E149.1.0.5", {"start": v(28.58, 374.65) * mm, "end": v(28.58, 381) * mm});
            skLineSegment(sketch, "E149.1.0.6", {"start": v(34.93, 381) * mm, "end": v(34.93, 387.35) * mm});
            skLineSegment(sketch, "E149.1.0.7", {"start": v(34.93, 387.35) * mm, "end": v(41.27, 387.35) * mm});
            skLineSegment(sketch, "E149.2.0.0", {"start": v(3.17, 387.35) * mm, "end": v(3.17, 381) * mm});
            skLineSegment(sketch, "E149.2.0.1", {"start": v(3.17, 381) * mm, "end": v(9.52, 381) * mm});
            skLineSegment(sketch, "E149.2.0.2", {"start": v(-9.52, 381) * mm, "end": v(-3.17, 381) * mm});
            skLineSegment(sketch, "E149.2.0.3", {"start": v(9.52, 381) * mm, "end": v(9.52, 374.65) * mm});
            skLineSegment(sketch, "E149.2.0.4", {"start": v(9.52, 374.65) * mm, "end": v(-9.52, 374.65) * mm});
            skLineSegment(sketch, "E149.2.0.5", {"start": v(-9.52, 374.65) * mm, "end": v(-9.52, 381) * mm});
            skLineSegment(sketch, "E149.2.0.6", {"start": v(-3.17, 381) * mm, "end": v(-3.17, 387.35) * mm});
            skLineSegment(sketch, "E149.2.0.7", {"start": v(-3.17, 387.35) * mm, "end": v(3.17, 387.35) * mm});
            skLineSegment(sketch, "E149.3.0.0", {"start": v(-34.93, 387.35) * mm, "end": v(-34.93, 381) * mm});
            skLineSegment(sketch, "E149.3.0.1", {"start": v(-34.93, 381) * mm, "end": v(-28.58, 381) * mm});
            skLineSegment(sketch, "E149.3.0.2", {"start": v(-47.62, 381) * mm, "end": v(-41.28, 381) * mm});
            skLineSegment(sketch, "E149.3.0.3", {"start": v(-28.58, 381) * mm, "end": v(-28.58, 374.65) * mm});
            skLineSegment(sketch, "E149.3.0.4", {"start": v(-28.58, 374.65) * mm, "end": v(-47.62, 374.65) * mm});
            skLineSegment(sketch, "E149.3.0.5", {"start": v(-47.62, 374.65) * mm, "end": v(-47.62, 381) * mm});
            skLineSegment(sketch, "E149.3.0.6", {"start": v(-41.28, 381) * mm, "end": v(-41.28, 387.35) * mm});
            skLineSegment(sketch, "E149.3.0.7", {"start": v(-41.28, 387.35) * mm, "end": v(-34.93, 387.35) * mm});
            skLineSegment(sketch, "E149.4.0.0", {"start": v(-73.02, 387.35) * mm, "end": v(-73.02, 381) * mm});
            skLineSegment(sketch, "E149.4.0.1", {"start": v(-73.03, 381) * mm, "end": v(-66.68, 381) * mm});
            skLineSegment(sketch, "E149.4.0.2", {"start": v(-85.72, 381) * mm, "end": v(-79.38, 381) * mm});
            skLineSegment(sketch, "E149.4.0.3", {"start": v(-66.67, 381) * mm, "end": v(-66.67, 374.65) * mm});
            skLineSegment(sketch, "E149.4.0.4", {"start": v(-66.68, 374.65) * mm, "end": v(-85.72, 374.65) * mm});
            skLineSegment(sketch, "E149.4.0.5", {"start": v(-85.72, 374.65) * mm, "end": v(-85.72, 381) * mm});
            skLineSegment(sketch, "E149.4.0.6", {"start": v(-79.37, 381) * mm, "end": v(-79.37, 387.35) * mm});
            skLineSegment(sketch, "E149.4.0.7", {"start": v(-79.38, 387.35) * mm, "end": v(-73.03, 387.35) * mm});
            skLineSegment(sketch, "E149.direction1", {"start": v(66.68, 374.65) * mm, "end": v(28.58, 374.65) * mm, "construction": true});
            skSolve(sketch);
        }
        {
            var Q0;
            Q0 = qSketchRegion(id + "F28", true);
            extrude(context, id + "F29", {"entities" : qUnion([Q0]), "operationType" : NewBodyOperationType.REMOVE, "endBound" : BoundingType.THROUGH_ALL, "oppositeDirection" : true, "depth" : 25.4 * mm, "offsetDistance" : 25.4 * mm, "hasSecondDirection" : true, "secondDirectionBound" : BoundingType.THROUGH_ALL, "secondDirectionOppositeDirection" : false, "secondDirectionDepth" : 25.4 * mm});
        }
        {
            var Q0;
            Q0=makeQuery(id+"F1.opExtrude","SWEPT_FACE",FACE,{"disambiguationData":[OSD([sQuery(id+"F0.wireOp",EDGE,"E11.right")])]});
            extrude(context, id + "F30", {"entities" : qUnion([Q0]), "operationType" : NewBodyOperationType.ADD, "depth" : 152.4 * mm, "offsetDistance" : 25.4 * mm});
        }
        {
            var Q0;
            Q0=makeQuery(id+"F30.opExtrude","CAP_FACE",FACE,{"disambiguationData":[OSD([sQuery(id+"F0.wireOp",EDGE,"E11.right")])],"isStart":false});
            var sketch = newSketch(context, id + "F31", { "sketchPlane" : qUnion([Q0])});
            skLineSegment(sketch, "E150.bottom", {"start": v(-762, -63.5) * mm, "end": v(762, -63.5) * mm});
            skLineSegment(sketch, "E150.top", {"start": v(-762, 1460.5) * mm, "end": v(762, 1460.5) * mm});
            skLineSegment(sketch, "E150.left", {"start": v(-762, -63.5) * mm, "end": v(-762, 1460.5) * mm});
            skLineSegment(sketch, "E150.right", {"start": v(762, -63.5) * mm, "end": v(762, 1460.5) * mm});
            skSolve(sketch);
        }
        {
            var Q0;
            Q0 = qSketchRegion(id + "F31", true);
            extrude(context, id + "F32", {"entities" : qUnion([Q0]), "operationType" : NewBodyOperationType.ADD, "depth" : 50.8 * mm, "offsetDistance" : 25.4 * mm});
        }
        {
            var Q0;
            Q0=makeQuery(id+"F32.opExtrude","SWEPT_FACE",FACE,{"disambiguationData":[OSD([sQuery(id+"F31.wireOp",EDGE,"E150.top")])]});
            var sketch = newSketch(context, id + "F33", { "sketchPlane" : qUnion([Q0])});
            skLineSegment(sketch, "E151", {"start": v(0, 762) * mm, "end": v(0, 812.8) * mm, "construction": true});
            skLineSegment(sketch, "E152", {"start": v(584.2, 762) * mm, "end": v(584.2, 749.3) * mm});
            skLineSegment(sketch, "E153", {"start": v(584.2, 749.3) * mm, "end": v(596.9, 749.3) * mm});
            skLineSegment(sketch, "E154", {"start": v(596.9, 749.3) * mm, "end": v(596.9, 736.6) * mm});
            skLineSegment(sketch, "E155", {"start": v(596.9, 736.6) * mm, "end": v(546.1, 736.6) * mm});
            skLineSegment(sketch, "E156", {"start": v(546.1, 736.6) * mm, "end": v(546.1, 749.3) * mm});
            skLineSegment(sketch, "E157", {"start": v(546.1, 749.3) * mm, "end": v(558.8, 749.3) * mm});
            skLineSegment(sketch, "E158", {"start": v(558.8, 749.3) * mm, "end": v(558.8, 762) * mm});
            skLineSegment(sketch, "E159", {"start": v(558.8, 762) * mm, "end": v(584.2, 762) * mm});
            skLineSegment(sketch, "E160.MirrorCS", {"start": v(-584.2, 749.3) * mm, "end": v(-596.9, 749.3) * mm});
            skLineSegment(sketch, "E161.MirrorCS", {"start": v(-558.8, 749.3) * mm, "end": v(-558.8, 762) * mm});
            skLineSegment(sketch, "E162.MirrorCS", {"start": v(-546.1, 749.3) * mm, "end": v(-558.8, 749.3) * mm});
            skLineSegment(sketch, "E163.MirrorCS", {"start": v(-546.1, 736.6) * mm, "end": v(-546.1, 749.3) * mm});
            skLineSegment(sketch, "E164.MirrorCS", {"start": v(-584.2, 762) * mm, "end": v(-584.2, 749.3) * mm});
            skLineSegment(sketch, "E165.MirrorCS", {"start": v(-596.9, 749.3) * mm, "end": v(-596.9, 736.6) * mm});
            skLineSegment(sketch, "E166.MirrorCS", {"start": v(-596.9, 736.6) * mm, "end": v(-546.1, 736.6) * mm});
            skLineSegment(sketch, "E167.MirrorCS", {"start": v(-558.8, 762) * mm, "end": v(-584.2, 762) * mm});
            skSolve(sketch);
        }
        {
            var Q0;
            Q0 = qSketchRegion(id + "F33", true);
            var Q1;
            {var subQ0=sQuery(id+"F0.wireOp",EDGE,"E11.right");var subQ1=sQuery(id+"F0.wireOp",EDGE,"E11.bottom");Q1=makeQuery(id+"F30.boolean.opBoolean","MERGE",FACE,{"derivedFrom":[makeQuery(id+"F1.opExtrude","SWEPT_FACE",FACE,{"disambiguationData":[OSD([subQ1]),TDD([makeQuery(id+"F0.imprint","IMPRINT",EDGE,{"disambiguationData":[TD([[makeQuery(id+"F0.imprint","INTERSECT",VERTEX,{"derivedFrom":[subQ1,subQ0]}),1.0]])],"derivedFrom":subQ1})])]}),makeQuery(id+"F30.opExtrude","SWEPT_FACE",FACE,{"disambiguationData":[OSD([subQ1,subQ0])]})]});}
            extrude(context, id + "F34", {"entities" : qUnion([Q0]), "operationType" : NewBodyOperationType.ADD, "endBound" : BoundingType.UP_TO_SURFACE, "oppositeDirection" : true, "depth" : 25.4 * mm, "endBoundEntityFace" : qUnion([Q1]), "offsetDistance" : 25.4 * mm});
        }
        {
            var Q0;
            Q0=makeQuery(id+"F34.boolean.opBoolean","MERGE",FACE,{"derivedFrom":[makeQuery(id+"F32.opExtrude","SWEPT_FACE",FACE,{"disambiguationData":[OSD([sQuery(id+"F31.wireOp",EDGE,"E150.top")])]}),makeQuery(id+"F34.opExtrude","CAP_FACE",FACE,{"disambiguationData":[OSD([sQuery(id+"F33.wireOp",EDGE,"E152"),sQuery(id+"F33.wireOp",EDGE,"E153"),sQuery(id+"F33.wireOp",EDGE,"E154"),sQuery(id+"F33.wireOp",EDGE,"E155"),sQuery(id+"F33.wireOp",EDGE,"E156"),sQuery(id+"F33.wireOp",EDGE,"E157"),sQuery(id+"F33.wireOp",EDGE,"E158"),sQuery(id+"F33.wireOp",EDGE,"E159")])],"isStart":true}),makeQuery(id+"F34.opExtrude","CAP_FACE",FACE,{"disambiguationData":[OSD([sQuery(id+"F33.wireOp",EDGE,"E160.MirrorCS"),sQuery(id+"F33.wireOp",EDGE,"E161.MirrorCS"),sQuery(id+"F33.wireOp",EDGE,"E162.MirrorCS"),sQuery(id+"F33.wireOp",EDGE,"E163.MirrorCS"),sQuery(id+"F33.wireOp",EDGE,"E164.MirrorCS"),sQuery(id+"F33.wireOp",EDGE,"E165.MirrorCS"),sQuery(id+"F33.wireOp",EDGE,"E166.MirrorCS"),sQuery(id+"F33.wireOp",EDGE,"E167.MirrorCS")])],"isStart":true})]});
            var sketch = newSketch(context, id + "F35", { "sketchPlane" : qUnion([Q0])});
            skLineSegment(sketch, "E168.0", {"start": v(584.2, 762) * mm, "end": v(584.2, 749.3) * mm});
            skLineSegment(sketch, "E169.0", {"start": v(584.2, 749.3) * mm, "end": v(596.9, 749.3) * mm});
            skLineSegment(sketch, "E170.0", {"start": v(596.9, 749.3) * mm, "end": v(596.9, 736.6) * mm});
            skLineSegment(sketch, "E171.0", {"start": v(596.9, 736.6) * mm, "end": v(546.1, 736.6) * mm});
            skLineSegment(sketch, "E172.0", {"start": v(546.1, 736.6) * mm, "end": v(546.1, 749.3) * mm});
            skLineSegment(sketch, "E173.0", {"start": v(546.1, 749.3) * mm, "end": v(558.8, 749.3) * mm});
            skLineSegment(sketch, "E174.0", {"start": v(558.8, 749.3) * mm, "end": v(558.8, 762) * mm});
            skLineSegment(sketch, "E175.0", {"start": v(-558.8, 749.3) * mm, "end": v(-558.8, 762) * mm});
            skLineSegment(sketch, "E176.0", {"start": v(-546.1, 749.3) * mm, "end": v(-558.8, 749.3) * mm});
            skLineSegment(sketch, "E177.0", {"start": v(-546.1, 736.6) * mm, "end": v(-546.1, 749.3) * mm});
            skLineSegment(sketch, "E178.0", {"start": v(-596.9, 736.6) * mm, "end": v(-546.1, 736.6) * mm});
            skLineSegment(sketch, "E179.0", {"start": v(-596.9, 749.3) * mm, "end": v(-596.9, 736.6) * mm});
            skLineSegment(sketch, "E180.0", {"start": v(-584.2, 749.3) * mm, "end": v(-596.9, 749.3) * mm});
            skLineSegment(sketch, "E181.0", {"start": v(-584.2, 762) * mm, "end": v(-584.2, 749.3) * mm});
            skLineSegment(sketch, "E182", {"start": v(-584.2, 762) * mm, "end": v(-609.6, 762) * mm});
            skLineSegment(sketch, "E183", {"start": v(-609.6, 762) * mm, "end": v(-609.6, 711.2) * mm});
            skLineSegment(sketch, "E184", {"start": v(-609.6, 711.2) * mm, "end": v(609.6, 711.2) * mm});
            skLineSegment(sketch, "E185", {"start": v(609.6, 711.2) * mm, "end": v(609.6, 762) * mm});
            skLineSegment(sketch, "E186", {"start": v(609.6, 762) * mm, "end": v(584.2, 762) * mm});
            skLineSegment(sketch, "E187", {"start": v(558.8, 762) * mm, "end": v(533.4, 762) * mm});
            skLineSegment(sketch, "E188", {"start": v(533.4, 762) * mm, "end": v(533.4, 736.6) * mm});
            skLineSegment(sketch, "E189", {"start": v(533.4, 736.6) * mm, "end": v(-533.4, 736.6) * mm});
            skLineSegment(sketch, "E190", {"start": v(-533.4, 736.6) * mm, "end": v(-533.4, 762) * mm});
            skLineSegment(sketch, "E191", {"start": v(-533.4, 762) * mm, "end": v(-558.8, 762) * mm});
            skSolve(sketch);
        }
        {
            var Q0;
            Q0 = qSketchRegion(id + "F35", true);
            extrude(context, id + "F36", {"entities" : qUnion([Q0]), "oppositeDirection" : true, "depth" : 457.2 * mm, "offsetDistance" : 25.4 * mm});
        }
        {
            var Q0;
            Q0=makeQuery(id+"F36.opExtrude","CAP_FACE",FACE,{"disambiguationData":[OSD([sQuery(id+"F35.wireOp",EDGE,"E168.0"),sQuery(id+"F35.wireOp",EDGE,"E169.0"),sQuery(id+"F35.wireOp",EDGE,"E170.0"),sQuery(id+"F35.wireOp",EDGE,"E171.0"),sQuery(id+"F35.wireOp",EDGE,"E172.0"),sQuery(id+"F35.wireOp",EDGE,"E173.0"),sQuery(id+"F35.wireOp",EDGE,"E174.0"),sQuery(id+"F35.wireOp",EDGE,"E175.0"),sQuery(id+"F35.wireOp",EDGE,"E176.0"),sQuery(id+"F35.wireOp",EDGE,"E177.0"),sQuery(id+"F35.wireOp",EDGE,"E178.0"),sQuery(id+"F35.wireOp",EDGE,"E179.0"),sQuery(id+"F35.wireOp",EDGE,"E180.0"),sQuery(id+"F35.wireOp",EDGE,"E181.0"),sQuery(id+"F35.wireOp",EDGE,"E182"),sQuery(id+"F35.wireOp",EDGE,"E183"),sQuery(id+"F35.wireOp",EDGE,"E184"),sQuery(id+"F35.wireOp",EDGE,"E185"),sQuery(id+"F35.wireOp",EDGE,"E186"),sQuery(id+"F35.wireOp",EDGE,"E187"),sQuery(id+"F35.wireOp",EDGE,"E188"),sQuery(id+"F35.wireOp",EDGE,"E189"),sQuery(id+"F35.wireOp",EDGE,"E190"),sQuery(id+"F35.wireOp",EDGE,"E191")])],"isStart":true});
            var sketch = newSketch(context, id + "F37", { "sketchPlane" : qUnion([Q0])});
            skArc(sketch, "E192.0", {"start": v(-95.21, -63.24) * mm, "mid": v(0, -114.3) * mm, "end": v(95.21, -63.24) * mm});
            skLineSegment(sketch, "E193", {"start": v(609.6, 711.2) * mm, "end": v(95.21, -63.24) * mm});
            skLineSegment(sketch, "E194", {"start": v(-609.6, 711.2) * mm, "end": v(-95.21, -63.24) * mm});
            skLineSegment(sketch, "E195", {"start": v(609.6, 711.2) * mm, "end": v(-609.6, 711.2) * mm});
            skSolve(sketch);
        }
        {
            var Q0;
            Q0 = qSketchRegion(id + "F37", true);
            var Q1;
            Q1=makeQuery(id+"F36.opExtrude","CAP_FACE",FACE,{"disambiguationData":[OSD([sQuery(id+"F35.wireOp",EDGE,"E168.0"),sQuery(id+"F35.wireOp",EDGE,"E169.0"),sQuery(id+"F35.wireOp",EDGE,"E170.0"),sQuery(id+"F35.wireOp",EDGE,"E171.0"),sQuery(id+"F35.wireOp",EDGE,"E172.0"),sQuery(id+"F35.wireOp",EDGE,"E173.0"),sQuery(id+"F35.wireOp",EDGE,"E174.0"),sQuery(id+"F35.wireOp",EDGE,"E175.0"),sQuery(id+"F35.wireOp",EDGE,"E176.0"),sQuery(id+"F35.wireOp",EDGE,"E177.0"),sQuery(id+"F35.wireOp",EDGE,"E178.0"),sQuery(id+"F35.wireOp",EDGE,"E179.0"),sQuery(id+"F35.wireOp",EDGE,"E180.0"),sQuery(id+"F35.wireOp",EDGE,"E181.0"),sQuery(id+"F35.wireOp",EDGE,"E182"),sQuery(id+"F35.wireOp",EDGE,"E183"),sQuery(id+"F35.wireOp",EDGE,"E184"),sQuery(id+"F35.wireOp",EDGE,"E185"),sQuery(id+"F35.wireOp",EDGE,"E186"),sQuery(id+"F35.wireOp",EDGE,"E187"),sQuery(id+"F35.wireOp",EDGE,"E188"),sQuery(id+"F35.wireOp",EDGE,"E189"),sQuery(id+"F35.wireOp",EDGE,"E190"),sQuery(id+"F35.wireOp",EDGE,"E191")])],"isStart":false});
            extrude(context, id + "F38", {"entities" : qUnion([Q0]), "operationType" : NewBodyOperationType.ADD, "endBound" : BoundingType.UP_TO_SURFACE, "oppositeDirection" : true, "depth" : 25.4 * mm, "endBoundEntityFace" : qUnion([Q1]), "offsetDistance" : 25.4 * mm});
        }
        {
            var Q0;
            Q0=makeQuery(id+"F38.boolean.opBoolean","MERGE",FACE,{"derivedFrom":[makeQuery(id+"F36.opExtrude","CAP_FACE",FACE,{"disambiguationData":[OSD([sQuery(id+"F35.wireOp",EDGE,"E168.0"),sQuery(id+"F35.wireOp",EDGE,"E169.0"),sQuery(id+"F35.wireOp",EDGE,"E170.0"),sQuery(id+"F35.wireOp",EDGE,"E171.0"),sQuery(id+"F35.wireOp",EDGE,"E172.0"),sQuery(id+"F35.wireOp",EDGE,"E173.0"),sQuery(id+"F35.wireOp",EDGE,"E174.0"),sQuery(id+"F35.wireOp",EDGE,"E175.0"),sQuery(id+"F35.wireOp",EDGE,"E176.0"),sQuery(id+"F35.wireOp",EDGE,"E177.0"),sQuery(id+"F35.wireOp",EDGE,"E178.0"),sQuery(id+"F35.wireOp",EDGE,"E179.0"),sQuery(id+"F35.wireOp",EDGE,"E180.0"),sQuery(id+"F35.wireOp",EDGE,"E181.0"),sQuery(id+"F35.wireOp",EDGE,"E182"),sQuery(id+"F35.wireOp",EDGE,"E183"),sQuery(id+"F35.wireOp",EDGE,"E184"),sQuery(id+"F35.wireOp",EDGE,"E185"),sQuery(id+"F35.wireOp",EDGE,"E186"),sQuery(id+"F35.wireOp",EDGE,"E187"),sQuery(id+"F35.wireOp",EDGE,"E188"),sQuery(id+"F35.wireOp",EDGE,"E189"),sQuery(id+"F35.wireOp",EDGE,"E190"),sQuery(id+"F35.wireOp",EDGE,"E191")])],"isStart":false}),makeQuery(id+"F38.opExtrude","CAP_FACE",FACE,{"disambiguationData":[OSD([sQuery(id+"F37.wireOp",EDGE,"E192.0"),sQuery(id+"F37.wireOp",EDGE,"E193"),sQuery(id+"F37.wireOp",EDGE,"E194"),sQuery(id+"F37.wireOp",EDGE,"E195")])],"isStart":false})]});
            var sketch = newSketch(context, id + "F39", { "sketchPlane" : qUnion([Q0])});
            skArc(sketch, "E196.0", {"start": v(95.21, 63.24) * mm, "mid": v(0, 114.3) * mm, "end": v(-95.21, 63.24) * mm, "construction": true});
            skCircle(sketch, "E197", {"center": v(0, 0) * mm, "radius": 50.8 * mm});
            skSolve(sketch);
        }
        {
            var Q0;
            Q0 = qSketchRegion(id + "F39", true);
            extrude(context, id + "F40", {"entities" : qUnion([Q0]), "operationType" : NewBodyOperationType.ADD, "depth" : 76.2 * mm, "offsetDistance" : 25.4 * mm});
        }
        {
            var Q0;
            Q0=qCreatedBy(makeId("Right.planeOp"),FACE);
            var sketch = newSketch(context, id + "F41", { "sketchPlane" : qUnion([Q0])});
            skLineSegment(sketch, "E198.0", {"start": v(50.8, 927.1) * mm, "end": v(-50.8, 927.1) * mm, "construction": true});
            skLineSegment(sketch, "E199", {"start": v(0, 927.1) * mm, "end": v(0, 825.5) * mm});
            skLineSegment(sketch, "E200", {"start": v(0, 825.5) * mm, "end": v(-50.8, 927.1) * mm});
            skLineSegment(sketch, "E201", {"start": v(-50.8, 927.1) * mm, "end": v(0, 927.1) * mm});
            skSolve(sketch);
        }
        {
            var Q0;
            Q0=makeQuery(id+"F41.imprint","IMPRINT",FACE,{"disambiguationData":[TD([[makeQuery(id+"F41.imprint","IMPRINT",EDGE,{"derivedFrom":sQuery(id+"F41.wireOp",EDGE,"E199")}),-1.0]])]});
            var Q1;
            Q1=sQuery(id+"F41.wireOp",EDGE,"E199");
            revolve(context, id + "F42", {"operationType" : NewBodyOperationType.ADD, "surfaceOperationType" : NewSurfaceOperationType.NEW, "entities" : qUnion([Q0]), "axis" : qUnion([Q1]), "revolveType" : RevolveType.FULL});
        }
        {
            var Q0;
            Q0=qCreatedBy(makeId("Front.planeOp"),FACE);
            var sketch = newSketch(context, id + "F43", { "sketchPlane" : qUnion([Q0])});
            skLineSegment(sketch, "E202.0", {"start": v(-79.38, 387.35) * mm, "end": v(-114.3, 387.35) * mm, "construction": true});
            skLineSegment(sketch, "E203", {"start": v(-19.66, 387.35) * mm, "end": v(-13.31, 387.35) * mm});
            skLineSegment(sketch, "E204", {"start": v(-13.31, 387.35) * mm, "end": v(-6.96, 393.7) * mm});
            skLineSegment(sketch, "E205", {"start": v(-6.96, 393.7) * mm, "end": v(5.74, 393.7) * mm});
            skLineSegment(sketch, "E206", {"start": v(5.74, 393.7) * mm, "end": v(12.09, 387.35) * mm});
            skLineSegment(sketch, "E207", {"start": v(12.09, 387.35) * mm, "end": v(18.44, 387.35) * mm});
            skLineSegment(sketch, "E208", {"start": v(18.44, 387.35) * mm, "end": v(18.44, 425.45) * mm});
            skLineSegment(sketch, "E209", {"start": v(18.44, 425.45) * mm, "end": v(-19.66, 425.45) * mm});
            skLineSegment(sketch, "E210", {"start": v(-19.66, 425.45) * mm, "end": v(-19.66, 387.35) * mm});
            skSolve(sketch);
        }
        {
            var Q0;
            Q0 = qSketchRegion(id + "F43", true);
            extrude(context, id + "F44", {"entities" : qUnion([Q0]), "depth" : 38.1 * mm, "offsetDistance" : 25.4 * mm});
        }
        {
            var Q0;
            Q0=makeQuery(id+"F44.opExtrude","SWEPT_FACE",FACE,{"disambiguationData":[OSD([sQuery(id+"F43.wireOp",EDGE,"E209")])]});
            var sketch = newSketch(context, id + "F45", { "sketchPlane" : qUnion([Q0])});
            skLineSegment(sketch, "E211", {"start": v(-19.66, 0) * mm, "end": v(18.44, -38.1) * mm, "construction": true});
            skCircle(sketch, "E212", {"center": v(-0.61, -19.05) * mm, "radius": 4.76 * mm});
            skSolve(sketch);
        }
        {
            var Q0;
            Q0 = qSketchRegion(id + "F45", true);
            extrude(context, id + "F46", {"entities" : qUnion([Q0]), "operationType" : NewBodyOperationType.ADD, "depth" : 101.6 * mm, "offsetDistance" : 25.4 * mm});
        }
        {
            var Q0;
            Q0=makeQuery(id+"F44.opExtrude","SWEPT_FACE",FACE,{"disambiguationData":[OSD([sQuery(id+"F43.wireOp",EDGE,"E209")])]});
            var sketch = newSketch(context, id + "F47", { "sketchPlane" : qUnion([Q0])});
            skLineSegment(sketch, "E213.bottom", {"start": v(-13.31, -6.35) * mm, "end": v(37.49, -6.35) * mm});
            skLineSegment(sketch, "E213.top", {"start": v(-13.31, -31.75) * mm, "end": v(37.49, -31.75) * mm});
            skLineSegment(sketch, "E213.left", {"start": v(-13.31, -6.35) * mm, "end": v(-13.31, -31.75) * mm});
            skLineSegment(sketch, "E213.right", {"start": v(37.49, -6.35) * mm, "end": v(37.49, -31.75) * mm});
            skLineSegment(sketch, "E214", {"start": v(-13.31, -6.35) * mm, "end": v(12.09, -31.75) * mm, "construction": true});
            skCircle(sketch, "E215.0", {"center": v(-0.61, -19.05) * mm, "radius": 4.76 * mm});
            skLineSegment(sketch, "E216.bottom", {"start": v(-13.31, -20.64) * mm, "end": v(12.09, -20.64) * mm});
            skLineSegment(sketch, "E216.top", {"start": v(-13.31, -17.46) * mm, "end": v(12.09, -17.46) * mm});
            skLineSegment(sketch, "E216.left", {"start": v(-13.31, -20.64) * mm, "end": v(-13.31, -17.46) * mm});
            skLineSegment(sketch, "E216.right", {"start": v(12.09, -20.64) * mm, "end": v(12.09, -17.46) * mm});
            skSolve(sketch);
        }
        {
            var Q0;
            {var subQ15=sQuery(id+"F47.wireOp",EDGE,"E216.right");Q0=makeQuery(id+"F47.imprint","IMPRINT",FACE,{"disambiguationData":[TD([[makeQuery(id+"F47.imprint","IMPRINT",EDGE,{"derivedFrom":subQ15}),-1.0]])]});}
            var Q1;
            {var subQ0=sQuery(id+"F47.wireOp",EDGE,"E213.right");Q1=makeQuery(id+"F47.imprint","IMPRINT",FACE,{"disambiguationData":[TD([[makeQuery(id+"F47.imprint","IMPRINT",EDGE,{"derivedFrom":subQ0}),-1.0]])]});}
            extrude(context, id + "F48", {"entities" : qUnion([Q0, Q1]), "depth" : 25.4 * mm, "offsetDistance" : 25.4 * mm});
        }
        {
            var Q0;
            Q0=makeQuery(id+"F48.opExtrude","SWEPT_FACE",FACE,{"disambiguationData":[OSD([sQuery(id+"F47.wireOp",EDGE,"E213.top")])]});
            var sketch = newSketch(context, id + "F49", { "sketchPlane" : qUnion([Q0])});
            skLineSegment(sketch, "E217", {"start": v(37.49, 450.85) * mm, "end": v(12.09, 425.45) * mm, "construction": true});
            skCircle(sketch, "E218", {"center": v(24.79, 438.15) * mm, "radius": 4.76 * mm});
            skLineSegment(sketch, "E219.bottom", {"start": v(37.49, 439.74) * mm, "end": v(12.09, 439.74) * mm});
            skLineSegment(sketch, "E219.top", {"start": v(37.49, 436.56) * mm, "end": v(12.09, 436.56) * mm});
            skLineSegment(sketch, "E219.left", {"start": v(37.49, 439.74) * mm, "end": v(37.49, 436.56) * mm});
            skLineSegment(sketch, "E219.right", {"start": v(12.09, 439.74) * mm, "end": v(12.09, 436.56) * mm});
            skSolve(sketch);
        }
        {
            var Q0;
            {var subQ0=sQuery(id+"F49.wireOp",EDGE,"E219.bottom");var subQ1=sQuery(id+"F49.wireOp",EDGE,"E218");var subQ2=makeQuery(id+"F49.imprint","INTERSECT",VERTEX,{"disambiguationData":[OD(0.0)],"derivedFrom":[subQ1,subQ0]});Q0=makeQuery(id+"F49.imprint","IMPRINT",FACE,{"disambiguationData":[TD([[makeQuery(id+"F49.imprint","IMPRINT",EDGE,{"disambiguationData":[TD([[subQ2,-1.0]])],"derivedFrom":subQ1}),1.0]])]});}
            var Q1;
            {var subQ0=sQuery(id+"F49.wireOp",EDGE,"E219.top");var subQ1=sQuery(id+"F49.wireOp",EDGE,"E218");var subQ2=makeQuery(id+"F49.imprint","INTERSECT",VERTEX,{"disambiguationData":[OD(0.0)],"derivedFrom":[subQ1,subQ0]});Q1=makeQuery(id+"F49.imprint","IMPRINT",FACE,{"disambiguationData":[TD([[makeQuery(id+"F49.imprint","IMPRINT",EDGE,{"disambiguationData":[TD([[subQ2,-1.0]])],"derivedFrom":subQ1}),1.0]])]});}
            var Q2;
            {var subQ0=sQuery(id+"F49.wireOp",EDGE,"E219.bottom");var subQ1=sQuery(id+"F49.wireOp",EDGE,"E218");var subQ2=makeQuery(id+"F49.imprint","INTERSECT",VERTEX,{"disambiguationData":[OD(0.0)],"derivedFrom":[subQ1,subQ0]});Q2=makeQuery(id+"F49.imprint","IMPRINT",FACE,{"disambiguationData":[TD([[makeQuery(id+"F49.imprint","IMPRINT",EDGE,{"disambiguationData":[TD([[subQ2,1.0]])],"derivedFrom":subQ1}),1.0]])]});}
            var Q3;
            {var subQ5=sQuery(id+"F49.wireOp",EDGE,"E219.right");Q3=makeQuery(id+"F49.imprint","IMPRINT",FACE,{"disambiguationData":[TD([[makeQuery(id+"F49.imprint","IMPRINT",EDGE,{"derivedFrom":subQ5}),1.0]])]});}
            var Q4;
            {var subQ5=sQuery(id+"F49.wireOp",EDGE,"E219.left");Q4=makeQuery(id+"F49.imprint","IMPRINT",FACE,{"disambiguationData":[TD([[makeQuery(id+"F49.imprint","IMPRINT",EDGE,{"derivedFrom":subQ5}),-1.0]])]});}
            extrude(context, id + "F50", {"entities" : qUnion([Q0, Q1, Q2, Q3, Q4]), "operationType" : NewBodyOperationType.REMOVE, "endBound" : BoundingType.THROUGH_ALL, "oppositeDirection" : true, "depth" : 25.4 * mm, "offsetDistance" : 25.4 * mm});
        }
        {
            var Q0;
            Q0=makeQuery(id+"F48.opExtrude","SWEPT_FACE",FACE,{"disambiguationData":[OSD([sQuery(id+"F47.wireOp",EDGE,"E213.bottom")])]});
            var sketch = newSketch(context, id + "F51", { "sketchPlane" : qUnion([Q0])});
            skArc(sketch, "E220.0", {"start": v(-29.28, 436.56) * mm, "mid": v(-24.79, 433.39) * mm, "end": v(-20.3, 436.56) * mm, "construction": true});
            skCircle(sketch, "E221", {"center": v(-24.79, 438.15) * mm, "radius": 4.76 * mm});
            skSolve(sketch);
        }
        {
            var Q0;
            Q0 = qSketchRegion(id + "F51", true);
            extrude(context, id + "F52", {"entities" : qUnion([Q0]), "oppositeDirection" : true, "depth" : 101.6 * mm, "offsetDistance" : 25.4 * mm});
        }
        {
            var Q0;
            Q0=makeQuery(id+"F44.opExtrude","SWEPT_FACE",FACE,{"disambiguationData":[OSD([sQuery(id+"F43.wireOp",EDGE,"E209")])]});
            var sketch = newSketch(context, id + "F53", { "sketchPlane" : qUnion([Q0])});
            skLineSegment(sketch, "E222.bottom", {"start": v(-10.99, -33.87) * mm, "end": v(9.76, -33.87) * mm});
            skLineSegment(sketch, "E222.top", {"start": v(-10.99, -4.23) * mm, "end": v(9.76, -4.23) * mm});
            skLineSegment(sketch, "E222.left", {"start": v(-10.99, -33.87) * mm, "end": v(-10.99, -4.23) * mm});
            skLineSegment(sketch, "E222.right", {"start": v(9.76, -33.87) * mm, "end": v(9.76, -4.23) * mm});
            skPoint(sketch, "E222.middle", {"position": v(-0.61, -19.05) * mm});
            skSolve(sketch);
        }
        {
            var Q0;
            Q0 = qSketchRegion(id + "F53", true);
            extrude(context, id + "F54", {"entities" : qUnion([Q0]), "operationType" : NewBodyOperationType.REMOVE, "endBound" : BoundingType.THROUGH_ALL, "depth" : 25.4 * mm, "offsetDistance" : 25.4 * mm});
        }
        {
            var Q0;
            Q0=makeQuery(id+"F52.opExtrude","CAP_FACE",FACE,{"disambiguationData":[OSD([sQuery(id+"F51.wireOp",EDGE,"E221")])],"isStart":false});
            var sketch = newSketch(context, id + "F55", { "sketchPlane" : qUnion([Q0])});
            skCircle(sketch, "E223.0.0", {"center": v(24.79, 438.15) * mm, "radius": 4.76 * mm});
            skPoint(sketch, "E224.0", {"position": v(37.49, 450.85) * mm});
            skLineSegment(sketch, "E225.bottom", {"start": v(37.49, 450.85) * mm, "end": v(12.09, 450.85) * mm});
            skLineSegment(sketch, "E225.top", {"start": v(37.49, 425.45) * mm, "end": v(12.09, 425.45) * mm});
            skLineSegment(sketch, "E225.left", {"start": v(37.49, 450.85) * mm, "end": v(37.49, 425.45) * mm});
            skLineSegment(sketch, "E225.right", {"start": v(12.09, 450.85) * mm, "end": v(12.09, 425.45) * mm});
            skSolve(sketch);
        }
        {
            var Q0;
            Q0 = qSketchRegion(id + "F55", true);
            extrude(context, id + "F56", {"entities" : qUnion([Q0]), "oppositeDirection" : true, "depth" : 25.4 * mm, "offsetDistance" : 25.4 * mm});
        }
        {
            var Q0;
            Q0=makeQuery(id+"F56.opExtrude","SWEPT_FACE",FACE,{"disambiguationData":[OSD([sQuery(id+"F55.wireOp",EDGE,"E225.left")])]});
            var sketch = newSketch(context, id + "F57", { "sketchPlane" : qUnion([Q0])});
            skLineSegment(sketch, "E226", {"start": v(-107.95, 425.45) * mm, "end": v(-82.55, 450.85) * mm, "construction": true});
            skCircle(sketch, "E227", {"center": v(-95.25, 438.15) * mm, "radius": 7.94 * mm});
            skSolve(sketch);
        }
        {
            var Q0;
            Q0 = qSketchRegion(id + "F57", true);
            extrude(context, id + "F58", {"entities" : qUnion([Q0]), "operationType" : NewBodyOperationType.ADD, "depth" : 9.52 * mm, "offsetDistance" : 25.4 * mm});
        }
        {
            var Q0;
            Q0=makeQuery(id+"F54.boolean.opBoolean","MERGE",FACE,{"derivedFrom":[makeQuery(id+"F44.opExtrude","SWEPT_FACE",FACE,{"disambiguationData":[OSD([sQuery(id+"F43.wireOp",EDGE,"E209")])]})],"fromTools":[makeQuery(id+"F54.opExtrude","CAP_FACE",FACE,{"disambiguationData":[OSD([sQuery(id+"F53.wireOp",EDGE,"E222.bottom"),sQuery(id+"F53.wireOp",EDGE,"E222.top"),sQuery(id+"F53.wireOp",EDGE,"E222.left"),sQuery(id+"F53.wireOp",EDGE,"E222.right")])],"isStart":true})]});
            var sketch = newSketch(context, id + "F59", { "sketchPlane" : qUnion([Q0])});
            skPoint(sketch, "E228.0", {"position": v(12.09, 0) * mm});
            skPoint(sketch, "E229.0", {"position": v(5.74, 0) * mm});
            skPoint(sketch, "E230.0", {"position": v(-6.96, 0) * mm});
            skPoint(sketch, "E231.0", {"position": v(-13.31, 0) * mm});
            skLineSegment(sketch, "E232", {"start": v(12.09, 0) * mm, "end": v(5.74, -6.35) * mm});
            skLineSegment(sketch, "E233", {"start": v(5.74, -6.35) * mm, "end": v(-6.96, -6.35) * mm});
            skLineSegment(sketch, "E234", {"start": v(-6.96, -6.35) * mm, "end": v(-13.31, 0) * mm});
            skLineSegment(sketch, "E235", {"start": v(12.09, 0) * mm, "end": v(-13.31, 0) * mm});
            skSolve(sketch);
        }
        {
            var Q0;
            Q0 = qSketchRegion(id + "F59", true);
            extrude(context, id + "F60", {"entities" : qUnion([Q0]), "operationType" : NewBodyOperationType.REMOVE, "endBound" : BoundingType.THROUGH_ALL, "oppositeDirection" : true, "depth" : 25.4 * mm, "offsetDistance" : 25.4 * mm});
        }
    });
